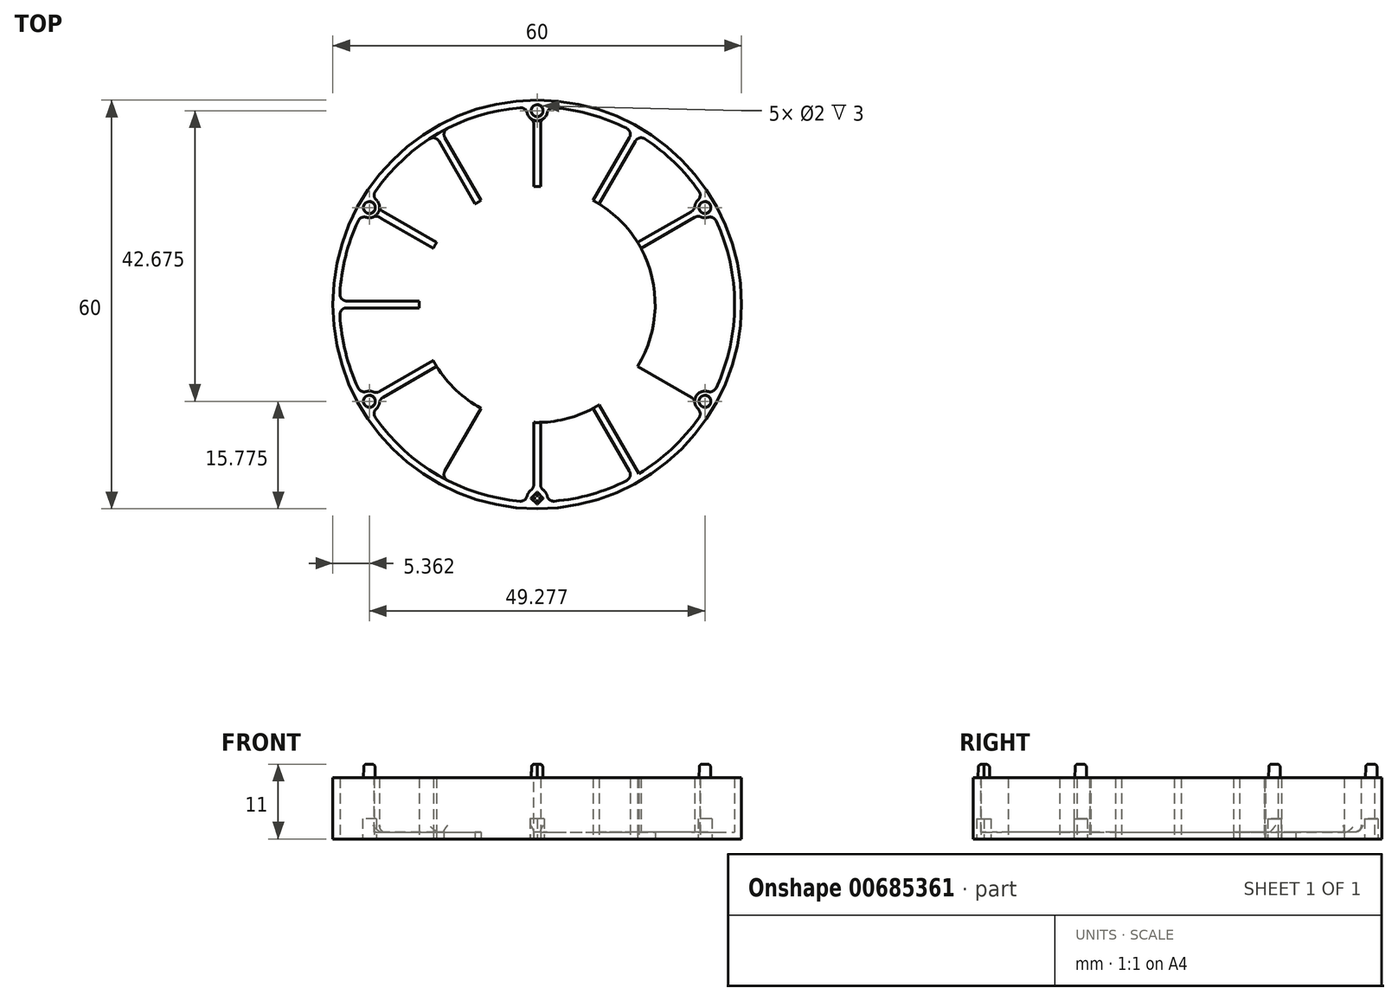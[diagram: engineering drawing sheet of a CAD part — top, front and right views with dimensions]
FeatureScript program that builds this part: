
annotation { "Feature Type Name" : "Feature", "Feature Type Description" : "" }
export const myFeature = defineFeature(function(context is Context, id is Id, definition is map)
    precondition{}
    {
        {
            var Q0;
            Q0=qCreatedBy(makeId("Top.planeOp"),FACE);
            var sketch = newSketch(context, id + "F0", { "sketchPlane" : qUnion([Q0])});
            skCircle(sketch, "E0", {"center": v(0, 0) * mm, "radius": 30 * mm});
            skCircle(sketch, "E1.0", {"center": v(0, 0) * mm, "radius": 29 * mm});
            skLineSegment(sketch, "E2.bottom", {"start": v(14.56, 26.23) * mm, "end": v(15.43, 25.73) * mm});
            skLineSegment(sketch, "E2.top", {"start": v(-15.43, -25.73) * mm, "end": v(-14.56, -26.23) * mm});
            skLineSegment(sketch, "E2.left", {"start": v(14.56, 26.23) * mm, "end": v(-15.43, -25.73) * mm});
            skLineSegment(sketch, "E2.right", {"start": v(15.43, 25.73) * mm, "end": v(-14.56, -26.23) * mm});
            skLineSegment(sketch, "E3.bottom", {"start": v(25.73, 15.43) * mm, "end": v(26.23, 14.56) * mm});
            skLineSegment(sketch, "E3.top", {"start": v(-26.23, -14.56) * mm, "end": v(-25.73, -15.43) * mm});
            skLineSegment(sketch, "E3.left", {"start": v(25.73, 15.43) * mm, "end": v(-26.23, -14.56) * mm});
            skLineSegment(sketch, "E3.right", {"start": v(26.23, 14.56) * mm, "end": v(-25.73, -15.43) * mm});
            skLineSegment(sketch, "E4", {"start": v(-38.35, 0) * mm, "end": v(39.17, 0) * mm, "construction": true});
            skLineSegment(sketch, "E5", {"start": v(0, 42.5) * mm, "end": v(0, -42.47) * mm, "construction": true});
            skLineSegment(sketch, "E6.bottom", {"start": v(-30, 0.5) * mm, "end": v(30, 0.5) * mm});
            skLineSegment(sketch, "E6.top", {"start": v(-30, -0.5) * mm, "end": v(30, -0.5) * mm});
            skLineSegment(sketch, "E6.left", {"start": v(-30, 0.5) * mm, "end": v(-30, -0.5) * mm});
            skLineSegment(sketch, "E6.right", {"start": v(30, 0.5) * mm, "end": v(30, -0.5) * mm});
            skLineSegment(sketch, "E7.bottom", {"start": v(-25.73, 15.43) * mm, "end": v(26.23, -14.56) * mm});
            skLineSegment(sketch, "E7.top", {"start": v(-26.23, 14.56) * mm, "end": v(25.73, -15.43) * mm});
            skLineSegment(sketch, "E7.left", {"start": v(-25.73, 15.43) * mm, "end": v(-26.23, 14.56) * mm});
            skLineSegment(sketch, "E7.right", {"start": v(26.23, -14.56) * mm, "end": v(25.73, -15.43) * mm});
            skLineSegment(sketch, "E8.bottom", {"start": v(-0.5, 30) * mm, "end": v(0.5, 30) * mm});
            skLineSegment(sketch, "E8.top", {"start": v(-0.5, -30) * mm, "end": v(0.5, -30) * mm});
            skLineSegment(sketch, "E8.left", {"start": v(-0.5, 30) * mm, "end": v(-0.5, -30) * mm});
            skLineSegment(sketch, "E8.right", {"start": v(0.5, 30) * mm, "end": v(0.5, -30) * mm});
            skLineSegment(sketch, "E9.bottom", {"start": v(-15.43, 25.73) * mm, "end": v(-14.56, 26.23) * mm});
            skLineSegment(sketch, "E9.top", {"start": v(14.56, -26.23) * mm, "end": v(15.43, -25.73) * mm});
            skLineSegment(sketch, "E9.left", {"start": v(-15.43, 25.73) * mm, "end": v(14.56, -26.23) * mm});
            skLineSegment(sketch, "E9.right", {"start": v(-14.56, 26.23) * mm, "end": v(15.43, -25.73) * mm});
            skCircle(sketch, "E10", {"center": v(0, 0) * mm, "radius": 17.33 * mm});
            skSolve(sketch);
        }
        {
            var Q0;
            Q0=qCreatedBy(makeId("Top.planeOp"),FACE);
            var sketch = newSketch(context, id + "F1", { "sketchPlane" : qUnion([Q0])});
            skCircle(sketch, "E11", {"center": v(0, 0) * mm, "radius": 30 * mm});
            skCircle(sketch, "E12", {"center": v(0, 0) * mm, "radius": 29 * mm});
            skSolve(sketch);
        }
        {
            var Q0;
            Q0=makeQuery(id+"F1.imprint","IMPRINT",FACE,{"disambiguationData":[TD([[makeQuery(id+"F1.imprint","IMPRINT",EDGE,{"derivedFrom":sQuery(id+"F1.wireOp",EDGE,"E11")}),1.0]])]});
            extrude(context, id + "F2", {"entities" : qUnion([Q0]), "depth" : 9 * mm, "offsetDistance" : 25 * mm});
        }
        {
            var Q0;
            {var subQ0=sQuery(id+"F0.wireOp",EDGE,"E2.right");var subQ1=sQuery(id+"F0.wireOp",EDGE,"E1.0");var subQ2=makeQuery(id+"F0.imprint","INTERSECT",VERTEX,{"disambiguationData":[OD(0.0)],"derivedFrom":[subQ1,subQ0]});Q0=makeQuery(id+"F0.imprint","IMPRINT",FACE,{"disambiguationData":[TD([[makeQuery(id+"F0.imprint","IMPRINT",EDGE,{"disambiguationData":[TD([[subQ2,-1.0]])],"derivedFrom":subQ1}),1.0]])]});}
            var Q1;
            {var subQ0=sQuery(id+"F0.wireOp",EDGE,"E8.left");var subQ1=sQuery(id+"F0.wireOp",EDGE,"E1.0");var subQ2=makeQuery(id+"F0.imprint","INTERSECT",VERTEX,{"disambiguationData":[OD(1.0)],"derivedFrom":[subQ1,subQ0]});Q1=makeQuery(id+"F0.imprint","IMPRINT",FACE,{"disambiguationData":[TD([[makeQuery(id+"F0.imprint","IMPRINT",EDGE,{"disambiguationData":[TD([[subQ2,-1.0]])],"derivedFrom":subQ1}),1.0]])]});}
            var Q2;
            {var subQ0=sQuery(id+"F0.wireOp",EDGE,"E3.left");var subQ1=sQuery(id+"F0.wireOp",EDGE,"E1.0");var subQ2=makeQuery(id+"F0.imprint","INTERSECT",VERTEX,{"disambiguationData":[OD(1.0)],"derivedFrom":[subQ1,subQ0]});Q2=makeQuery(id+"F0.imprint","IMPRINT",FACE,{"disambiguationData":[TD([[makeQuery(id+"F0.imprint","IMPRINT",EDGE,{"disambiguationData":[TD([[subQ2,-1.0]])],"derivedFrom":subQ1}),1.0]])]});}
            var Q3;
            {var subQ0=sQuery(id+"F0.wireOp",EDGE,"E3.right");var subQ1=sQuery(id+"F0.wireOp",EDGE,"E1.0");var subQ2=makeQuery(id+"F0.imprint","INTERSECT",VERTEX,{"disambiguationData":[OD(0.0)],"derivedFrom":[subQ1,subQ0]});Q3=makeQuery(id+"F0.imprint","IMPRINT",FACE,{"disambiguationData":[TD([[makeQuery(id+"F0.imprint","IMPRINT",EDGE,{"disambiguationData":[TD([[subQ2,-1.0]])],"derivedFrom":subQ1}),1.0]])]});}
            var Q4;
            {var subQ0=sQuery(id+"F0.wireOp",EDGE,"E9.left");var subQ1=sQuery(id+"F0.wireOp",EDGE,"E1.0");var subQ2=makeQuery(id+"F0.imprint","INTERSECT",VERTEX,{"disambiguationData":[OD(1.0)],"derivedFrom":[subQ1,subQ0]});Q4=makeQuery(id+"F0.imprint","IMPRINT",FACE,{"disambiguationData":[TD([[makeQuery(id+"F0.imprint","IMPRINT",EDGE,{"disambiguationData":[TD([[subQ2,-1.0]])],"derivedFrom":subQ1}),1.0]])]});}
            var Q5;
            {var subQ0=sQuery(id+"F0.wireOp",EDGE,"E6.bottom");var subQ1=sQuery(id+"F0.wireOp",EDGE,"E1.0");var subQ2=makeQuery(id+"F0.imprint","INTERSECT",VERTEX,{"disambiguationData":[OD(1.0)],"derivedFrom":[subQ1,subQ0]});Q5=makeQuery(id+"F0.imprint","IMPRINT",FACE,{"disambiguationData":[TD([[makeQuery(id+"F0.imprint","IMPRINT",EDGE,{"disambiguationData":[TD([[subQ2,-1.0]])],"derivedFrom":subQ1}),1.0]])]});}
            extrude(context, id + "F3", {"entities" : qUnion([Q0, Q1, Q2, Q3, Q4, Q5]), "operationType" : NewBodyOperationType.ADD, "depth" : 9 * mm, "offsetDistance" : 25 * mm});
        }
        {
            var Q0;
            Q0=makeQuery(id+"F1.imprint","IMPRINT",FACE,{"disambiguationData":[TD([[makeQuery(id+"F1.imprint","IMPRINT",EDGE,{"derivedFrom":sQuery(id+"F1.wireOp",EDGE,"E11")}),1.0]])]});
            var Q1;
            Q1=makeQuery(id+"F1.imprint","IMPRINT",FACE,{"disambiguationData":[TD([[makeQuery(id+"F1.imprint","IMPRINT",EDGE,{"derivedFrom":sQuery(id+"F1.wireOp",EDGE,"E12")}),1.0]])]});
            extrude(context, id + "F4", {"entities" : qUnion([Q0, Q1]), "operationType" : NewBodyOperationType.ADD, "depth" : 1 * mm, "offsetDistance" : 25 * mm});
        }
        {
            var Q0;
            {var subQ0=sQuery(id+"F0.wireOp",EDGE,"E9.right");var subQ1=sQuery(id+"F0.wireOp",EDGE,"E1.0");var subQ2=makeQuery(id+"F0.imprint","INTERSECT",VERTEX,{"disambiguationData":[OD(1.0)],"derivedFrom":[subQ1,subQ0]});Q0=makeQuery(id+"F0.imprint","IMPRINT",FACE,{"disambiguationData":[TD([[makeQuery(id+"F0.imprint","IMPRINT",EDGE,{"disambiguationData":[TD([[subQ2,-1.0]])],"derivedFrom":subQ1}),1.0]])]});}
            var Q1;
            {var subQ0=sQuery(id+"F0.wireOp",EDGE,"E2.left");var subQ1=sQuery(id+"F0.wireOp",EDGE,"E1.0");var subQ2=makeQuery(id+"F0.imprint","INTERSECT",VERTEX,{"disambiguationData":[OD(0.0)],"derivedFrom":[subQ1,subQ0]});Q1=makeQuery(id+"F0.imprint","IMPRINT",FACE,{"disambiguationData":[TD([[makeQuery(id+"F0.imprint","IMPRINT",EDGE,{"disambiguationData":[TD([[subQ2,-1.0]])],"derivedFrom":subQ1}),1.0]])]});}
            var Q2;
            {var subQ0=sQuery(id+"F0.wireOp",EDGE,"E2.right");var subQ1=sQuery(id+"F0.wireOp",EDGE,"E1.0");var subQ2=makeQuery(id+"F0.imprint","INTERSECT",VERTEX,{"disambiguationData":[OD(1.0)],"derivedFrom":[subQ1,subQ0]});Q2=makeQuery(id+"F0.imprint","IMPRINT",FACE,{"disambiguationData":[TD([[makeQuery(id+"F0.imprint","IMPRINT",EDGE,{"disambiguationData":[TD([[subQ2,-1.0]])],"derivedFrom":subQ1}),1.0]])]});}
            var Q3;
            {var subQ0=sQuery(id+"F0.wireOp",EDGE,"E8.left");var subQ1=sQuery(id+"F0.wireOp",EDGE,"E1.0");var subQ2=makeQuery(id+"F0.imprint","INTERSECT",VERTEX,{"disambiguationData":[OD(0.0)],"derivedFrom":[subQ1,subQ0]});Q3=makeQuery(id+"F0.imprint","IMPRINT",FACE,{"disambiguationData":[TD([[makeQuery(id+"F0.imprint","IMPRINT",EDGE,{"disambiguationData":[TD([[subQ2,-1.0]])],"derivedFrom":subQ1}),1.0]])]});}
            var Q4;
            {var subQ0=sQuery(id+"F0.wireOp",EDGE,"E9.left");var subQ1=sQuery(id+"F0.wireOp",EDGE,"E1.0");var subQ2=makeQuery(id+"F0.imprint","INTERSECT",VERTEX,{"disambiguationData":[OD(0.0)],"derivedFrom":[subQ1,subQ0]});Q4=makeQuery(id+"F0.imprint","IMPRINT",FACE,{"disambiguationData":[TD([[makeQuery(id+"F0.imprint","IMPRINT",EDGE,{"disambiguationData":[TD([[subQ2,-1.0]])],"derivedFrom":subQ1}),1.0]])]});}
            var Q5;
            {var subQ0=sQuery(id+"F0.wireOp",EDGE,"E7.top");var subQ1=sQuery(id+"F0.wireOp",EDGE,"E1.0");var subQ2=makeQuery(id+"F0.imprint","INTERSECT",VERTEX,{"disambiguationData":[OD(0.0)],"derivedFrom":[subQ1,subQ0]});Q5=makeQuery(id+"F0.imprint","IMPRINT",FACE,{"disambiguationData":[TD([[makeQuery(id+"F0.imprint","IMPRINT",EDGE,{"disambiguationData":[TD([[subQ2,-1.0]])],"derivedFrom":subQ1}),1.0]])]});}
            var Q6;
            {var subQ0=sQuery(id+"F0.wireOp",EDGE,"E6.top");var subQ1=sQuery(id+"F0.wireOp",EDGE,"E1.0");var subQ2=makeQuery(id+"F0.imprint","INTERSECT",VERTEX,{"disambiguationData":[OD(0.0)],"derivedFrom":[subQ1,subQ0]});Q6=makeQuery(id+"F0.imprint","IMPRINT",FACE,{"disambiguationData":[TD([[makeQuery(id+"F0.imprint","IMPRINT",EDGE,{"disambiguationData":[TD([[subQ2,-1.0]])],"derivedFrom":subQ1}),1.0]])]});}
            extrude(context, id + "F5", {"entities" : qUnion([Q0, Q1, Q2, Q3, Q4, Q5, Q6]), "operationType" : NewBodyOperationType.REMOVE, "depth" : 1 * mm, "offsetDistance" : 25 * mm});
        }
        {
            var Q0;
            Q0=qCreatedBy(makeId("Top.planeOp"),FACE);
            var sketch = newSketch(context, id + "F6", { "sketchPlane" : qUnion([Q0])});
            skCircle(sketch, "E13", {"center": v(0, 0) * mm, "radius": 28.45 * mm});
            skLineSegment(sketch, "E14", {"start": v(0, 28.45) * mm, "end": v(0, -28.45) * mm, "construction": true});
            skLineSegment(sketch, "E15", {"start": v(24.64, 14.22) * mm, "end": v(0, 0) * mm, "construction": true});
            skLineSegment(sketch, "E16", {"start": v(14.23, 24.64) * mm, "end": v(0, 0) * mm, "construction": true});
            skLineSegment(sketch, "E17", {"start": v(0, 0) * mm, "end": v(28.45, 0) * mm, "construction": true});
            skLineSegment(sketch, "E18", {"start": v(0, 0) * mm, "end": v(24.64, -14.22) * mm, "construction": true});
            skLineSegment(sketch, "E19", {"start": v(0, 0) * mm, "end": v(14.23, -24.64) * mm, "construction": true});
            skLineSegment(sketch, "E20", {"start": v(0, 0) * mm, "end": v(-14.23, 24.64) * mm, "construction": true});
            skLineSegment(sketch, "E21", {"start": v(0, 0) * mm, "end": v(-24.64, 14.22) * mm, "construction": true});
            skLineSegment(sketch, "E22", {"start": v(0, 0) * mm, "end": v(-28.45, 0) * mm, "construction": true});
            skLineSegment(sketch, "E23", {"start": v(0, 0) * mm, "end": v(-24.64, -14.23) * mm, "construction": true});
            skLineSegment(sketch, "E24", {"start": v(0, 0) * mm, "end": v(-14.22, -24.64) * mm, "construction": true});
            skCircle(sketch, "E25", {"center": v(0, 28.45) * mm, "radius": 1.5 * mm});
            skCircle(sketch, "E26", {"center": v(24.64, 14.22) * mm, "radius": 1.5 * mm});
            skCircle(sketch, "E27", {"center": v(24.64, -14.22) * mm, "radius": 1.5 * mm});
            skCircle(sketch, "E28", {"center": v(0, -28.45) * mm, "radius": 1.5 * mm});
            skCircle(sketch, "E29", {"center": v(-24.64, -14.23) * mm, "radius": 1.5 * mm});
            skCircle(sketch, "E30", {"center": v(-24.64, 14.22) * mm, "radius": 1.5 * mm});
            skCircle(sketch, "E31", {"center": v(-24.64, 14.22) * mm, "radius": 1 * mm});
            skCircle(sketch, "E32", {"center": v(0, 28.45) * mm, "radius": 1 * mm});
            skCircle(sketch, "E33", {"center": v(24.64, 14.22) * mm, "radius": 1 * mm});
            skCircle(sketch, "E34", {"center": v(24.64, -14.22) * mm, "radius": 1 * mm});
            skCircle(sketch, "E35", {"center": v(-24.64, -14.23) * mm, "radius": 1 * mm});
            skLineSegment(sketch, "E36.bottom", {"start": v(1.06, -28.45) * mm, "end": v(0, -29.51) * mm});
            skLineSegment(sketch, "E36.top", {"start": v(0, -27.39) * mm, "end": v(-1.06, -28.45) * mm});
            skLineSegment(sketch, "E36.left", {"start": v(1.06, -28.45) * mm, "end": v(0, -27.39) * mm});
            skLineSegment(sketch, "E36.right", {"start": v(0, -29.51) * mm, "end": v(-1.06, -28.45) * mm});
            skSolve(sketch);
        }
        {
            var Q0;
            {var subQ0=sQuery(id+"F6.wireOp",EDGE,"E30");var subQ1=sQuery(id+"F6.wireOp",EDGE,"E13");var subQ2=makeQuery(id+"F6.imprint","INTERSECT",VERTEX,{"disambiguationData":[OD(0.0)],"derivedFrom":[subQ1,subQ0]});Q0=makeQuery(id+"F6.imprint","IMPRINT",FACE,{"disambiguationData":[TD([[makeQuery(id+"F6.imprint","IMPRINT",EDGE,{"disambiguationData":[TD([[subQ2,-1.0]])],"derivedFrom":subQ1}),1.0]])]});}
            var Q1;
            {var subQ0=sQuery(id+"F6.wireOp",EDGE,"E30");var subQ1=sQuery(id+"F6.wireOp",EDGE,"E13");var subQ2=makeQuery(id+"F6.imprint","INTERSECT",VERTEX,{"disambiguationData":[OD(0.0)],"derivedFrom":[subQ1,subQ0]});Q1=makeQuery(id+"F6.imprint","IMPRINT",FACE,{"disambiguationData":[TD([[makeQuery(id+"F6.imprint","IMPRINT",EDGE,{"disambiguationData":[TD([[subQ2,-1.0]])],"derivedFrom":subQ1}),-1.0]])]});}
            var Q2;
            {var subQ0=sQuery(id+"F6.wireOp",EDGE,"E25");var subQ1=sQuery(id+"F6.wireOp",EDGE,"E13");var subQ2=makeQuery(id+"F6.imprint","INTERSECT",VERTEX,{"disambiguationData":[OD(0.0)],"derivedFrom":[subQ1,subQ0]});Q2=makeQuery(id+"F6.imprint","IMPRINT",FACE,{"disambiguationData":[TD([[makeQuery(id+"F6.imprint","IMPRINT",EDGE,{"disambiguationData":[TD([[subQ2,-1.0]])],"derivedFrom":subQ1}),1.0]])]});}
            var Q3;
            {var subQ0=sQuery(id+"F6.wireOp",EDGE,"E25");var subQ1=sQuery(id+"F6.wireOp",EDGE,"E13");var subQ2=makeQuery(id+"F6.imprint","INTERSECT",VERTEX,{"disambiguationData":[OD(0.0)],"derivedFrom":[subQ1,subQ0]});Q3=makeQuery(id+"F6.imprint","IMPRINT",FACE,{"disambiguationData":[TD([[makeQuery(id+"F6.imprint","IMPRINT",EDGE,{"disambiguationData":[TD([[subQ2,-1.0]])],"derivedFrom":subQ1}),-1.0]])]});}
            var Q4;
            {var subQ0=sQuery(id+"F6.wireOp",EDGE,"E26");var subQ1=sQuery(id+"F6.wireOp",EDGE,"E13");var subQ2=makeQuery(id+"F6.imprint","INTERSECT",VERTEX,{"disambiguationData":[OD(0.0)],"derivedFrom":[subQ1,subQ0]});Q4=makeQuery(id+"F6.imprint","IMPRINT",FACE,{"disambiguationData":[TD([[makeQuery(id+"F6.imprint","IMPRINT",EDGE,{"disambiguationData":[TD([[subQ2,-1.0]])],"derivedFrom":subQ1}),-1.0]])]});}
            var Q5;
            {var subQ0=sQuery(id+"F6.wireOp",EDGE,"E26");var subQ1=sQuery(id+"F6.wireOp",EDGE,"E13");var subQ2=makeQuery(id+"F6.imprint","INTERSECT",VERTEX,{"disambiguationData":[OD(0.0)],"derivedFrom":[subQ1,subQ0]});Q5=makeQuery(id+"F6.imprint","IMPRINT",FACE,{"disambiguationData":[TD([[makeQuery(id+"F6.imprint","IMPRINT",EDGE,{"disambiguationData":[TD([[subQ2,-1.0]])],"derivedFrom":subQ1}),1.0]])]});}
            var Q6;
            {var subQ0=sQuery(id+"F6.wireOp",EDGE,"E29");var subQ1=sQuery(id+"F6.wireOp",EDGE,"E13");var subQ2=makeQuery(id+"F6.imprint","INTERSECT",VERTEX,{"disambiguationData":[OD(0.0)],"derivedFrom":[subQ1,subQ0]});Q6=makeQuery(id+"F6.imprint","IMPRINT",FACE,{"disambiguationData":[TD([[makeQuery(id+"F6.imprint","IMPRINT",EDGE,{"disambiguationData":[TD([[subQ2,-1.0]])],"derivedFrom":subQ1}),1.0]])]});}
            var Q7;
            {var subQ0=sQuery(id+"F6.wireOp",EDGE,"E29");var subQ1=sQuery(id+"F6.wireOp",EDGE,"E13");var subQ2=makeQuery(id+"F6.imprint","INTERSECT",VERTEX,{"disambiguationData":[OD(0.0)],"derivedFrom":[subQ1,subQ0]});Q7=makeQuery(id+"F6.imprint","IMPRINT",FACE,{"disambiguationData":[TD([[makeQuery(id+"F6.imprint","IMPRINT",EDGE,{"disambiguationData":[TD([[subQ2,-1.0]])],"derivedFrom":subQ1}),-1.0]])]});}
            var Q8;
            {var subQ3=sQuery(id+"F6.wireOp",EDGE,"E13");var subQ5=sQuery(id+"F6.wireOp",EDGE,"E28");var subQ6=makeQuery(id+"F6.imprint","INTERSECT",VERTEX,{"disambiguationData":[OD(0.0)],"derivedFrom":[subQ3,subQ5]});Q8=makeQuery(id+"F6.imprint","IMPRINT",FACE,{"disambiguationData":[TD([[makeQuery(id+"F6.imprint","IMPRINT",EDGE,{"disambiguationData":[TD([[subQ6,-1.0]])],"derivedFrom":subQ3}),1.0]])]});}
            var Q9;
            {var subQ6=sQuery(id+"F6.wireOp",EDGE,"E36.bottom");Q9=makeQuery(id+"F6.imprint","IMPRINT",FACE,{"disambiguationData":[TD([[makeQuery(id+"F6.imprint","IMPRINT",EDGE,{"derivedFrom":subQ6}),1.0]])]});}
            var Q10;
            {var subQ0=sQuery(id+"F6.wireOp",EDGE,"E27");var subQ1=sQuery(id+"F6.wireOp",EDGE,"E13");var subQ2=makeQuery(id+"F6.imprint","INTERSECT",VERTEX,{"disambiguationData":[OD(0.0)],"derivedFrom":[subQ1,subQ0]});Q10=makeQuery(id+"F6.imprint","IMPRINT",FACE,{"disambiguationData":[TD([[makeQuery(id+"F6.imprint","IMPRINT",EDGE,{"disambiguationData":[TD([[subQ2,-1.0]])],"derivedFrom":subQ1}),-1.0]])]});}
            var Q11;
            {var subQ0=sQuery(id+"F6.wireOp",EDGE,"E27");var subQ1=sQuery(id+"F6.wireOp",EDGE,"E13");var subQ2=makeQuery(id+"F6.imprint","INTERSECT",VERTEX,{"disambiguationData":[OD(0.0)],"derivedFrom":[subQ1,subQ0]});Q11=makeQuery(id+"F6.imprint","IMPRINT",FACE,{"disambiguationData":[TD([[makeQuery(id+"F6.imprint","IMPRINT",EDGE,{"disambiguationData":[TD([[subQ2,-1.0]])],"derivedFrom":subQ1}),1.0]])]});}
            var Q12;
            {var subQ0=sQuery(id+"F6.wireOp",EDGE,"E31");var subQ1=sQuery(id+"F6.wireOp",EDGE,"E13");var subQ2=makeQuery(id+"F6.imprint","INTERSECT",VERTEX,{"disambiguationData":[OD(0.0)],"derivedFrom":[subQ1,subQ0]});Q12=makeQuery(id+"F6.imprint","IMPRINT",FACE,{"disambiguationData":[TD([[makeQuery(id+"F6.imprint","IMPRINT",EDGE,{"disambiguationData":[TD([[subQ2,-1.0]])],"derivedFrom":subQ1}),1.0]])]});}
            var Q13;
            {var subQ0=sQuery(id+"F6.wireOp",EDGE,"E31");var subQ1=sQuery(id+"F6.wireOp",EDGE,"E13");var subQ2=makeQuery(id+"F6.imprint","INTERSECT",VERTEX,{"disambiguationData":[OD(0.0)],"derivedFrom":[subQ1,subQ0]});Q13=makeQuery(id+"F6.imprint","IMPRINT",FACE,{"disambiguationData":[TD([[makeQuery(id+"F6.imprint","IMPRINT",EDGE,{"disambiguationData":[TD([[subQ2,-1.0]])],"derivedFrom":subQ1}),-1.0]])]});}
            var Q14;
            {var subQ0=sQuery(id+"F6.wireOp",EDGE,"E32");var subQ1=sQuery(id+"F6.wireOp",EDGE,"E13");var subQ2=makeQuery(id+"F6.imprint","INTERSECT",VERTEX,{"disambiguationData":[OD(0.0)],"derivedFrom":[subQ1,subQ0]});Q14=makeQuery(id+"F6.imprint","IMPRINT",FACE,{"disambiguationData":[TD([[makeQuery(id+"F6.imprint","IMPRINT",EDGE,{"disambiguationData":[TD([[subQ2,-1.0]])],"derivedFrom":subQ1}),-1.0]])]});}
            var Q15;
            {var subQ0=sQuery(id+"F6.wireOp",EDGE,"E32");var subQ1=sQuery(id+"F6.wireOp",EDGE,"E13");var subQ2=makeQuery(id+"F6.imprint","INTERSECT",VERTEX,{"disambiguationData":[OD(0.0)],"derivedFrom":[subQ1,subQ0]});Q15=makeQuery(id+"F6.imprint","IMPRINT",FACE,{"disambiguationData":[TD([[makeQuery(id+"F6.imprint","IMPRINT",EDGE,{"disambiguationData":[TD([[subQ2,-1.0]])],"derivedFrom":subQ1}),1.0]])]});}
            var Q16;
            {var subQ0=sQuery(id+"F6.wireOp",EDGE,"E33");var subQ1=sQuery(id+"F6.wireOp",EDGE,"E13");var subQ2=makeQuery(id+"F6.imprint","INTERSECT",VERTEX,{"disambiguationData":[OD(0.0)],"derivedFrom":[subQ1,subQ0]});Q16=makeQuery(id+"F6.imprint","IMPRINT",FACE,{"disambiguationData":[TD([[makeQuery(id+"F6.imprint","IMPRINT",EDGE,{"disambiguationData":[TD([[subQ2,-1.0]])],"derivedFrom":subQ1}),-1.0]])]});}
            var Q17;
            {var subQ0=sQuery(id+"F6.wireOp",EDGE,"E33");var subQ1=sQuery(id+"F6.wireOp",EDGE,"E13");var subQ2=makeQuery(id+"F6.imprint","INTERSECT",VERTEX,{"disambiguationData":[OD(0.0)],"derivedFrom":[subQ1,subQ0]});Q17=makeQuery(id+"F6.imprint","IMPRINT",FACE,{"disambiguationData":[TD([[makeQuery(id+"F6.imprint","IMPRINT",EDGE,{"disambiguationData":[TD([[subQ2,-1.0]])],"derivedFrom":subQ1}),1.0]])]});}
            var Q18;
            {var subQ0=sQuery(id+"F6.wireOp",EDGE,"E34");var subQ1=sQuery(id+"F6.wireOp",EDGE,"E13");var subQ2=makeQuery(id+"F6.imprint","INTERSECT",VERTEX,{"disambiguationData":[OD(0.0)],"derivedFrom":[subQ1,subQ0]});Q18=makeQuery(id+"F6.imprint","IMPRINT",FACE,{"disambiguationData":[TD([[makeQuery(id+"F6.imprint","IMPRINT",EDGE,{"disambiguationData":[TD([[subQ2,-1.0]])],"derivedFrom":subQ1}),-1.0]])]});}
            var Q19;
            {var subQ0=sQuery(id+"F6.wireOp",EDGE,"E34");var subQ1=sQuery(id+"F6.wireOp",EDGE,"E13");var subQ2=makeQuery(id+"F6.imprint","INTERSECT",VERTEX,{"disambiguationData":[OD(0.0)],"derivedFrom":[subQ1,subQ0]});Q19=makeQuery(id+"F6.imprint","IMPRINT",FACE,{"disambiguationData":[TD([[makeQuery(id+"F6.imprint","IMPRINT",EDGE,{"disambiguationData":[TD([[subQ2,-1.0]])],"derivedFrom":subQ1}),1.0]])]});}
            var Q20;
            {var subQ1=sQuery(id+"F6.wireOp",EDGE,"E36.bottom");Q20=makeQuery(id+"F6.imprint","IMPRINT",FACE,{"disambiguationData":[TD([[makeQuery(id+"F6.imprint","IMPRINT",EDGE,{"derivedFrom":subQ1}),-1.0]])]});}
            var Q21;
            {var subQ0=sQuery(id+"F6.wireOp",EDGE,"E35");var subQ1=sQuery(id+"F6.wireOp",EDGE,"E13");var subQ2=makeQuery(id+"F6.imprint","INTERSECT",VERTEX,{"disambiguationData":[OD(0.0)],"derivedFrom":[subQ1,subQ0]});Q21=makeQuery(id+"F6.imprint","IMPRINT",FACE,{"disambiguationData":[TD([[makeQuery(id+"F6.imprint","IMPRINT",EDGE,{"disambiguationData":[TD([[subQ2,-1.0]])],"derivedFrom":subQ1}),-1.0]])]});}
            var Q22;
            {var subQ0=sQuery(id+"F6.wireOp",EDGE,"E35");var subQ1=sQuery(id+"F6.wireOp",EDGE,"E13");var subQ2=makeQuery(id+"F6.imprint","INTERSECT",VERTEX,{"disambiguationData":[OD(0.0)],"derivedFrom":[subQ1,subQ0]});Q22=makeQuery(id+"F6.imprint","IMPRINT",FACE,{"disambiguationData":[TD([[makeQuery(id+"F6.imprint","IMPRINT",EDGE,{"disambiguationData":[TD([[subQ2,-1.0]])],"derivedFrom":subQ1}),1.0]])]});}
            var Q23;
            {var subQ0=sQuery(id+"F6.wireOp",EDGE,"E36.top");var subQ1=sQuery(id+"F6.wireOp",EDGE,"E13");var subQ2=makeQuery(id+"F6.imprint","INTERSECT",VERTEX,{"derivedFrom":[subQ1,subQ0]});Q23=makeQuery(id+"F6.imprint","IMPRINT",FACE,{"disambiguationData":[TD([[makeQuery(id+"F6.imprint","IMPRINT",EDGE,{"disambiguationData":[TD([[subQ2,-1.0]])],"derivedFrom":subQ1}),1.0]])]});}
            extrude(context, id + "F7", {"entities" : qUnion([Q0, Q1, Q2, Q3, Q4, Q5, Q6, Q7, Q8, Q9, Q10, Q11, Q12, Q13, Q14, Q15, Q16, Q17, Q18, Q19, Q20, Q21, Q22, Q23]), "operationType" : NewBodyOperationType.ADD, "depth" : 9 * mm, "offsetDistance" : 25 * mm});
        }
        {
            var Q0;
            {var subQ0=sQuery(id+"F0.wireOp",EDGE,"E8.right");var subQ1=sQuery(id+"F0.wireOp",EDGE,"E1.0");Q0=makeQuery(id+"F3.opExtrude","SWEPT_EDGE",EDGE,{"disambiguationData":[OSD([subQ1,subQ0]),TDD([makeQuery(id+"F0.imprint","INTERSECT",VERTEX,{"disambiguationData":[OD(1.0)],"derivedFrom":[subQ1,subQ0]})])]});}
            var Q1;
            {var subQ0=sQuery(id+"F0.wireOp",EDGE,"E2.left");var subQ1=sQuery(id+"F0.wireOp",EDGE,"E1.0");Q1=makeQuery(id+"F3.opExtrude","SWEPT_EDGE",EDGE,{"disambiguationData":[OSD([subQ1,subQ0]),TDD([makeQuery(id+"F0.imprint","INTERSECT",VERTEX,{"disambiguationData":[OD(1.0)],"derivedFrom":[subQ1,subQ0]})])]});}
            var Q2;
            {var subQ0=sQuery(id+"F0.wireOp",EDGE,"E3.left");var subQ1=sQuery(id+"F0.wireOp",EDGE,"E1.0");Q2=makeQuery(id+"F3.opExtrude","SWEPT_EDGE",EDGE,{"disambiguationData":[OSD([subQ1,subQ0]),TDD([makeQuery(id+"F0.imprint","INTERSECT",VERTEX,{"disambiguationData":[OD(1.0)],"derivedFrom":[subQ1,subQ0]})])]});}
            var Q3;
            {var subQ0=sQuery(id+"F0.wireOp",EDGE,"E6.bottom");var subQ1=sQuery(id+"F0.wireOp",EDGE,"E1.0");Q3=makeQuery(id+"F3.opExtrude","SWEPT_EDGE",EDGE,{"disambiguationData":[OSD([subQ1,subQ0]),TDD([makeQuery(id+"F0.imprint","INTERSECT",VERTEX,{"disambiguationData":[OD(1.0)],"derivedFrom":[subQ1,subQ0]})])]});}
            var Q4;
            {var subQ0=sQuery(id+"F0.wireOp",EDGE,"E9.right");var subQ1=sQuery(id+"F0.wireOp",EDGE,"E1.0");Q4=makeQuery(id+"F3.opExtrude","SWEPT_EDGE",EDGE,{"disambiguationData":[OSD([subQ1,subQ0]),TDD([makeQuery(id+"F0.imprint","INTERSECT",VERTEX,{"disambiguationData":[OD(1.0)],"derivedFrom":[subQ1,subQ0]})])]});}
            var Q5;
            {var subQ0=sQuery(id+"F0.wireOp",EDGE,"E7.bottom");var subQ1=sQuery(id+"F0.wireOp",EDGE,"E1.0");Q5=makeQuery(id+"F3.opExtrude","SWEPT_EDGE",EDGE,{"disambiguationData":[OSD([subQ1,subQ0]),TDD([makeQuery(id+"F0.imprint","INTERSECT",VERTEX,{"disambiguationData":[OD(1.0)],"derivedFrom":[subQ1,subQ0]})])]});}
            var Q6;
            {var subQ0=sQuery(id+"F0.wireOp",EDGE,"E8.left");var subQ1=sQuery(id+"F0.wireOp",EDGE,"E1.0");Q6=makeQuery(id+"F3.opExtrude","SWEPT_EDGE",EDGE,{"disambiguationData":[OSD([subQ1,subQ0]),TDD([makeQuery(id+"F0.imprint","INTERSECT",VERTEX,{"disambiguationData":[OD(0.0)],"derivedFrom":[subQ1,subQ0]})])]});}
            var Q7;
            {var subQ0=sQuery(id+"F0.wireOp",EDGE,"E2.left");var subQ1=sQuery(id+"F0.wireOp",EDGE,"E1.0");Q7=makeQuery(id+"F3.opExtrude","SWEPT_EDGE",EDGE,{"disambiguationData":[OSD([subQ1,subQ0]),TDD([makeQuery(id+"F0.imprint","INTERSECT",VERTEX,{"disambiguationData":[OD(0.0)],"derivedFrom":[subQ1,subQ0]})])]});}
            var Q8;
            {var subQ0=sQuery(id+"F0.wireOp",EDGE,"E3.left");var subQ1=sQuery(id+"F0.wireOp",EDGE,"E1.0");Q8=makeQuery(id+"F3.opExtrude","SWEPT_EDGE",EDGE,{"disambiguationData":[OSD([subQ1,subQ0]),TDD([makeQuery(id+"F0.imprint","INTERSECT",VERTEX,{"disambiguationData":[OD(0.0)],"derivedFrom":[subQ1,subQ0]})])]});}
            var Q9;
            {var subQ0=sQuery(id+"F0.wireOp",EDGE,"E6.top");var subQ1=sQuery(id+"F0.wireOp",EDGE,"E1.0");Q9=makeQuery(id+"F3.opExtrude","SWEPT_EDGE",EDGE,{"disambiguationData":[OSD([subQ1,subQ0]),TDD([makeQuery(id+"F0.imprint","INTERSECT",VERTEX,{"disambiguationData":[OD(1.0)],"derivedFrom":[subQ1,subQ0]})])]});}
            var Q10;
            {var subQ0=sQuery(id+"F0.wireOp",EDGE,"E7.top");var subQ1=sQuery(id+"F0.wireOp",EDGE,"E1.0");Q10=makeQuery(id+"F3.opExtrude","SWEPT_EDGE",EDGE,{"disambiguationData":[OSD([subQ1,subQ0]),TDD([makeQuery(id+"F0.imprint","INTERSECT",VERTEX,{"disambiguationData":[OD(0.0)],"derivedFrom":[subQ1,subQ0]})])]});}
            var Q11;
            {var subQ0=sQuery(id+"F0.wireOp",EDGE,"E6.top");var subQ1=sQuery(id+"F0.wireOp",EDGE,"E1.0");Q11=makeQuery(id+"F3.opExtrude","SWEPT_EDGE",EDGE,{"disambiguationData":[OSD([subQ1,subQ0]),TDD([makeQuery(id+"F0.imprint","INTERSECT",VERTEX,{"disambiguationData":[OD(0.0)],"derivedFrom":[subQ1,subQ0]})])]});}
            var Q12;
            {var subQ0=sQuery(id+"F0.wireOp",EDGE,"E9.left");var subQ1=sQuery(id+"F0.wireOp",EDGE,"E1.0");Q12=makeQuery(id+"F3.opExtrude","SWEPT_EDGE",EDGE,{"disambiguationData":[OSD([subQ1,subQ0]),TDD([makeQuery(id+"F0.imprint","INTERSECT",VERTEX,{"disambiguationData":[OD(0.0)],"derivedFrom":[subQ1,subQ0]})])]});}
            var Q13;
            {var subQ0=sQuery(id+"F0.wireOp",EDGE,"E8.right");var subQ1=sQuery(id+"F0.wireOp",EDGE,"E1.0");Q13=makeQuery(id+"F3.opExtrude","SWEPT_EDGE",EDGE,{"disambiguationData":[OSD([subQ1,subQ0]),TDD([makeQuery(id+"F0.imprint","INTERSECT",VERTEX,{"disambiguationData":[OD(0.0)],"derivedFrom":[subQ1,subQ0]})])]});}
            var Q14;
            {var subQ0=sQuery(id+"F0.wireOp",EDGE,"E7.bottom");var subQ1=sQuery(id+"F0.wireOp",EDGE,"E1.0");Q14=makeQuery(id+"F3.opExtrude","SWEPT_EDGE",EDGE,{"disambiguationData":[OSD([subQ1,subQ0]),TDD([makeQuery(id+"F0.imprint","INTERSECT",VERTEX,{"disambiguationData":[OD(0.0)],"derivedFrom":[subQ1,subQ0]})])]});}
            var Q15;
            {var subQ0=sQuery(id+"F0.wireOp",EDGE,"E9.right");var subQ1=sQuery(id+"F0.wireOp",EDGE,"E1.0");Q15=makeQuery(id+"F3.opExtrude","SWEPT_EDGE",EDGE,{"disambiguationData":[OSD([subQ1,subQ0]),TDD([makeQuery(id+"F0.imprint","INTERSECT",VERTEX,{"disambiguationData":[OD(0.0)],"derivedFrom":[subQ1,subQ0]})])]});}
            var Q16;
            {var subQ0=sQuery(id+"F0.wireOp",EDGE,"E3.right");var subQ1=sQuery(id+"F0.wireOp",EDGE,"E1.0");Q16=makeQuery(id+"F3.opExtrude","SWEPT_EDGE",EDGE,{"disambiguationData":[OSD([subQ1,subQ0]),TDD([makeQuery(id+"F0.imprint","INTERSECT",VERTEX,{"disambiguationData":[OD(1.0)],"derivedFrom":[subQ1,subQ0]})])]});}
            var Q17;
            {var subQ0=sQuery(id+"F0.wireOp",EDGE,"E2.right");var subQ1=sQuery(id+"F0.wireOp",EDGE,"E1.0");Q17=makeQuery(id+"F3.opExtrude","SWEPT_EDGE",EDGE,{"disambiguationData":[OSD([subQ1,subQ0]),TDD([makeQuery(id+"F0.imprint","INTERSECT",VERTEX,{"disambiguationData":[OD(1.0)],"derivedFrom":[subQ1,subQ0]})])]});}
            var Q18;
            {var subQ0=sQuery(id+"F0.wireOp",EDGE,"E3.right");var subQ1=sQuery(id+"F0.wireOp",EDGE,"E1.0");Q18=makeQuery(id+"F3.opExtrude","SWEPT_EDGE",EDGE,{"disambiguationData":[OSD([subQ1,subQ0]),TDD([makeQuery(id+"F0.imprint","INTERSECT",VERTEX,{"disambiguationData":[OD(0.0)],"derivedFrom":[subQ1,subQ0]})])]});}
            var Q19;
            {var subQ0=sQuery(id+"F0.wireOp",EDGE,"E2.right");var subQ1=sQuery(id+"F0.wireOp",EDGE,"E1.0");Q19=makeQuery(id+"F3.opExtrude","SWEPT_EDGE",EDGE,{"disambiguationData":[OSD([subQ1,subQ0]),TDD([makeQuery(id+"F0.imprint","INTERSECT",VERTEX,{"disambiguationData":[OD(0.0)],"derivedFrom":[subQ1,subQ0]})])]});}
            var Q20;
            {var subQ0=sQuery(id+"F0.wireOp",EDGE,"E8.left");var subQ1=sQuery(id+"F0.wireOp",EDGE,"E1.0");Q20=makeQuery(id+"F3.opExtrude","SWEPT_EDGE",EDGE,{"disambiguationData":[OSD([subQ1,subQ0]),TDD([makeQuery(id+"F0.imprint","INTERSECT",VERTEX,{"disambiguationData":[OD(1.0)],"derivedFrom":[subQ1,subQ0]})])]});}
            var Q21;
            {var subQ0=sQuery(id+"F0.wireOp",EDGE,"E9.left");var subQ1=sQuery(id+"F0.wireOp",EDGE,"E1.0");Q21=makeQuery(id+"F3.opExtrude","SWEPT_EDGE",EDGE,{"disambiguationData":[OSD([subQ1,subQ0]),TDD([makeQuery(id+"F0.imprint","INTERSECT",VERTEX,{"disambiguationData":[OD(1.0)],"derivedFrom":[subQ1,subQ0]})])]});}
            var Q22;
            {var subQ0=sQuery(id+"F0.wireOp",EDGE,"E7.top");var subQ1=sQuery(id+"F0.wireOp",EDGE,"E1.0");Q22=makeQuery(id+"F3.opExtrude","SWEPT_EDGE",EDGE,{"disambiguationData":[OSD([subQ1,subQ0]),TDD([makeQuery(id+"F0.imprint","INTERSECT",VERTEX,{"disambiguationData":[OD(1.0)],"derivedFrom":[subQ1,subQ0]})])]});}
            var Q23;
            {var subQ0=sQuery(id+"F0.wireOp",EDGE,"E6.bottom");var subQ1=sQuery(id+"F0.wireOp",EDGE,"E1.0");Q23=makeQuery(id+"F3.opExtrude","SWEPT_EDGE",EDGE,{"disambiguationData":[OSD([subQ1,subQ0]),TDD([makeQuery(id+"F0.imprint","INTERSECT",VERTEX,{"disambiguationData":[OD(0.0)],"derivedFrom":[subQ1,subQ0]})])]});}
            var Q24;
            {var subQ17=sQuery(id+"F0.wireOp",EDGE,"E8.right");var subQ18=sQuery(id+"F1.wireOp",EDGE,"E12");Q24=makeQuery(id+"F7.boolean.opBoolean","INTERSECT",EDGE,{"derivedFrom":[makeQuery(id+"F3.boolean.opBoolean","SPLIT",FACE,{"disambiguationData":[TD([makeQuery(id+"F3.opExtrude","SWEPT_FACE",FACE,{"disambiguationData":[OSD([subQ17])]})])],"derivedFrom":makeQuery(id+"F2.opExtrude","SWEPT_FACE",FACE,{"disambiguationData":[OSD([subQ18])]})}),makeQuery(id+"F7.opExtrude","SWEPT_FACE",FACE,{"disambiguationData":[OSD([sQuery(id+"F6.wireOp",EDGE,"E28")])]})]});}
            var Q25;
            {var subQ0=sQuery(id+"F0.wireOp",EDGE,"E6.top");var subQ1=sQuery(id+"F0.wireOp",EDGE,"E1.0");var subQ16=sQuery(id+"F1.wireOp",EDGE,"E12");Q25=makeQuery(id+"F7.boolean.opBoolean","INTERSECT",EDGE,{"derivedFrom":[makeQuery(id+"F5.boolean.opBoolean","MERGE",FACE,{"derivedFrom":[makeQuery(id+"F3.boolean.opBoolean","SPLIT",FACE,{"disambiguationData":[TD([makeQuery(id+"F3.opExtrude","SWEPT_FACE",FACE,{"disambiguationData":[OSD([subQ0])]})])],"derivedFrom":makeQuery(id+"F2.opExtrude","SWEPT_FACE",FACE,{"disambiguationData":[OSD([subQ16])]})}),makeQuery(id+"F5.opExtrude","SWEPT_FACE",FACE,{"disambiguationData":[OSD([subQ1]),TDD([makeQuery(id+"F0.imprint","IMPRINT",EDGE,{"disambiguationData":[TD([[makeQuery(id+"F0.imprint","INTERSECT",VERTEX,{"disambiguationData":[OD(0.0)],"derivedFrom":[subQ1,subQ0]}),-1.0]])],"derivedFrom":subQ1})])]})]}),makeQuery(id+"F7.opExtrude","SWEPT_FACE",FACE,{"disambiguationData":[OSD([sQuery(id+"F6.wireOp",EDGE,"E29")])]})]});}
            var Q26;
            Q26=makeQuery(id+"F7.boolean.opBoolean","INTERSECT",EDGE,{"derivedFrom":[makeQuery(id+"F3.opExtrude","SWEPT_FACE",FACE,{"disambiguationData":[OSD([sQuery(id+"F0.wireOp",EDGE,"E8.right")])]}),makeQuery(id+"F7.opExtrude","SWEPT_FACE",FACE,{"disambiguationData":[OSD([sQuery(id+"F6.wireOp",EDGE,"E28")])]})]});
            var Q27;
            {var subQ0=sQuery(id+"F0.wireOp",EDGE,"E3.left");Q27=makeQuery(id+"F7.boolean.opBoolean","INTERSECT",EDGE,{"derivedFrom":[makeQuery(id+"F5.boolean.opBoolean","MERGE",FACE,{"derivedFrom":[makeQuery(id+"F3.opExtrude","SWEPT_FACE",FACE,{"disambiguationData":[OSD([subQ0]),TDD([makeQuery(id+"F0.imprint","IMPRINT",EDGE,{"disambiguationData":[TD([[makeQuery(id+"F0.imprint","INTERSECT",VERTEX,{"disambiguationData":[OD(1.0)],"derivedFrom":[sQuery(id+"F0.wireOp",EDGE,"E1.0"),subQ0]}),1.0]])],"derivedFrom":subQ0})])]}),makeQuery(id+"F5.opExtrude","SWEPT_FACE",FACE,{"disambiguationData":[OSD([subQ0])]})]}),makeQuery(id+"F7.opExtrude","SWEPT_FACE",FACE,{"disambiguationData":[OSD([sQuery(id+"F6.wireOp",EDGE,"E29")])]})]});}
            var Q28;
            {var subQ0=sQuery(id+"F0.wireOp",EDGE,"E9.right");var subQ1=sQuery(id+"F0.wireOp",EDGE,"E1.0");var subQ17=sQuery(id+"F1.wireOp",EDGE,"E12");Q28=makeQuery(id+"F7.boolean.opBoolean","INTERSECT",EDGE,{"disambiguationData":[OD(0.0)],"derivedFrom":[makeQuery(id+"F5.boolean.opBoolean","MERGE",FACE,{"derivedFrom":[makeQuery(id+"F3.boolean.opBoolean","SPLIT",FACE,{"disambiguationData":[TD([makeQuery(id+"F3.opExtrude","SWEPT_FACE",FACE,{"disambiguationData":[OSD([subQ0])]})])],"derivedFrom":makeQuery(id+"F2.opExtrude","SWEPT_FACE",FACE,{"disambiguationData":[OSD([subQ17])]})}),makeQuery(id+"F5.opExtrude","SWEPT_FACE",FACE,{"disambiguationData":[OSD([subQ1]),TDD([makeQuery(id+"F0.imprint","IMPRINT",EDGE,{"disambiguationData":[TD([[makeQuery(id+"F0.imprint","INTERSECT",VERTEX,{"disambiguationData":[OD(1.0)],"derivedFrom":[subQ1,subQ0]}),-1.0]])],"derivedFrom":subQ1})])]})]}),makeQuery(id+"F7.opExtrude","SWEPT_FACE",FACE,{"disambiguationData":[OSD([sQuery(id+"F6.wireOp",EDGE,"E27")])]})]});}
            var Q29;
            {var subQ0=sQuery(id+"F0.wireOp",EDGE,"E9.right");var subQ1=sQuery(id+"F0.wireOp",EDGE,"E1.0");var subQ17=sQuery(id+"F1.wireOp",EDGE,"E12");Q29=makeQuery(id+"F7.boolean.opBoolean","INTERSECT",EDGE,{"derivedFrom":[makeQuery(id+"F5.boolean.opBoolean","MERGE",FACE,{"derivedFrom":[makeQuery(id+"F3.boolean.opBoolean","SPLIT",FACE,{"disambiguationData":[TD([makeQuery(id+"F3.opExtrude","SWEPT_FACE",FACE,{"disambiguationData":[OSD([subQ0])]})])],"derivedFrom":makeQuery(id+"F2.opExtrude","SWEPT_FACE",FACE,{"disambiguationData":[OSD([subQ17])]})}),makeQuery(id+"F5.opExtrude","SWEPT_FACE",FACE,{"disambiguationData":[OSD([subQ1]),TDD([makeQuery(id+"F0.imprint","IMPRINT",EDGE,{"disambiguationData":[TD([[makeQuery(id+"F0.imprint","INTERSECT",VERTEX,{"disambiguationData":[OD(1.0)],"derivedFrom":[subQ1,subQ0]}),-1.0]])],"derivedFrom":subQ1})])]})]}),makeQuery(id+"F7.opExtrude","SWEPT_FACE",FACE,{"disambiguationData":[OSD([sQuery(id+"F6.wireOp",EDGE,"E26")])]})]});}
            var Q30;
            {var subQ0=sQuery(id+"F0.wireOp",EDGE,"E1.0");var subQ2=sQuery(id+"F0.wireOp",EDGE,"E9.left");var subQ3=sQuery(id+"F0.wireOp",EDGE,"E8.left");var subQ5=sQuery(id+"F0.wireOp",EDGE,"E2.left");var subQ20=sQuery(id+"F1.wireOp",EDGE,"E12");Q30=makeQuery(id+"F7.boolean.opBoolean","INTERSECT",EDGE,{"disambiguationData":[OD(1.0)],"derivedFrom":[makeQuery(id+"F5.boolean.opBoolean","MERGE",FACE,{"derivedFrom":[makeQuery(id+"F3.boolean.opBoolean","SPLIT",FACE,{"disambiguationData":[TD([makeQuery(id+"F3.opExtrude","SWEPT_FACE",FACE,{"disambiguationData":[OSD([subQ5])]})])],"derivedFrom":makeQuery(id+"F2.opExtrude","SWEPT_FACE",FACE,{"disambiguationData":[OSD([subQ20])]})}),makeQuery(id+"F5.opExtrude","SWEPT_FACE",FACE,{"disambiguationData":[OSD([subQ0]),TDD([makeQuery(id+"F0.imprint","IMPRINT",EDGE,{"disambiguationData":[TD([[makeQuery(id+"F0.imprint","INTERSECT",VERTEX,{"disambiguationData":[OD(0.0)],"derivedFrom":[subQ0,subQ5]}),-1.0]])],"derivedFrom":subQ0})])]}),makeQuery(id+"F5.opExtrude","SWEPT_FACE",FACE,{"disambiguationData":[OSD([subQ0]),TDD([makeQuery(id+"F0.imprint","IMPRINT",EDGE,{"disambiguationData":[TD([[makeQuery(id+"F0.imprint","INTERSECT",VERTEX,{"disambiguationData":[OD(0.0)],"derivedFrom":[subQ0,subQ3]}),-1.0]])],"derivedFrom":subQ0})])]}),makeQuery(id+"F5.opExtrude","SWEPT_FACE",FACE,{"disambiguationData":[OSD([subQ0]),TDD([makeQuery(id+"F0.imprint","IMPRINT",EDGE,{"disambiguationData":[TD([[makeQuery(id+"F0.imprint","INTERSECT",VERTEX,{"disambiguationData":[OD(0.0)],"derivedFrom":[subQ0,subQ2]}),-1.0]])],"derivedFrom":subQ0})])]}),makeQuery(id+"F5.opExtrude","SWEPT_FACE",FACE,{"disambiguationData":[OSD([subQ0]),TDD([makeQuery(id+"F0.imprint","IMPRINT",EDGE,{"disambiguationData":[TD([[makeQuery(id+"F0.imprint","INTERSECT",VERTEX,{"disambiguationData":[OD(0.0)],"derivedFrom":[subQ0,sQuery(id+"F0.wireOp",EDGE,"E7.top")]}),-1.0]])],"derivedFrom":subQ0})])]})]}),makeQuery(id+"F7.opExtrude","SWEPT_FACE",FACE,{"disambiguationData":[OSD([sQuery(id+"F6.wireOp",EDGE,"E25")])]})]});}
            var Q31;
            {var subQ0=sQuery(id+"F0.wireOp",EDGE,"E8.left");Q31=makeQuery(id+"F7.boolean.opBoolean","INTERSECT",EDGE,{"derivedFrom":[makeQuery(id+"F5.boolean.opBoolean","COPY",FACE,{"derivedFrom":makeQuery(id+"F5.opExtrude","SWEPT_FACE",FACE,{"disambiguationData":[OSD([subQ0]),TDD([makeQuery(id+"F0.imprint","IMPRINT",EDGE,{"disambiguationData":[TD([[makeQuery(id+"F0.imprint","INTERSECT",VERTEX,{"disambiguationData":[OD(0.0)],"derivedFrom":[sQuery(id+"F0.wireOp",EDGE,"E1.0"),subQ0]}),-1.0]])],"derivedFrom":subQ0})])]})}),makeQuery(id+"F7.opExtrude","SWEPT_FACE",FACE,{"disambiguationData":[OSD([sQuery(id+"F6.wireOp",EDGE,"E25")])]})]});}
            var Q32;
            {var subQ0=sQuery(id+"F0.wireOp",EDGE,"E3.left");Q32=makeQuery(id+"F7.boolean.opBoolean","INTERSECT",EDGE,{"derivedFrom":[makeQuery(id+"F3.opExtrude","SWEPT_FACE",FACE,{"disambiguationData":[OSD([subQ0]),TDD([makeQuery(id+"F0.imprint","IMPRINT",EDGE,{"disambiguationData":[TD([[makeQuery(id+"F0.imprint","INTERSECT",VERTEX,{"disambiguationData":[OD(0.0)],"derivedFrom":[sQuery(id+"F0.wireOp",EDGE,"E1.0"),subQ0]}),-1.0]])],"derivedFrom":subQ0})])]}),makeQuery(id+"F7.opExtrude","SWEPT_FACE",FACE,{"disambiguationData":[OSD([sQuery(id+"F6.wireOp",EDGE,"E26")])]})]});}
            var Q33;
            {var subQ14=sQuery(id+"F0.wireOp",EDGE,"E2.right");var subQ16=sQuery(id+"F1.wireOp",EDGE,"E12");Q33=makeQuery(id+"F7.boolean.opBoolean","INTERSECT",EDGE,{"derivedFrom":[makeQuery(id+"F3.boolean.opBoolean","SPLIT",FACE,{"disambiguationData":[TD([makeQuery(id+"F3.opExtrude","SWEPT_FACE",FACE,{"disambiguationData":[OSD([subQ14])]})])],"derivedFrom":makeQuery(id+"F2.opExtrude","SWEPT_FACE",FACE,{"disambiguationData":[OSD([subQ16])]})}),makeQuery(id+"F7.opExtrude","SWEPT_FACE",FACE,{"disambiguationData":[OSD([sQuery(id+"F6.wireOp",EDGE,"E26")])]})]});}
            var Q34;
            {var subQ0=sQuery(id+"F0.wireOp",EDGE,"E1.0");var subQ2=sQuery(id+"F0.wireOp",EDGE,"E9.left");var subQ3=sQuery(id+"F0.wireOp",EDGE,"E8.left");var subQ5=sQuery(id+"F0.wireOp",EDGE,"E2.left");var subQ20=sQuery(id+"F1.wireOp",EDGE,"E12");Q34=makeQuery(id+"F7.boolean.opBoolean","INTERSECT",EDGE,{"disambiguationData":[OD(0.0)],"derivedFrom":[makeQuery(id+"F5.boolean.opBoolean","MERGE",FACE,{"derivedFrom":[makeQuery(id+"F3.boolean.opBoolean","SPLIT",FACE,{"disambiguationData":[TD([makeQuery(id+"F3.opExtrude","SWEPT_FACE",FACE,{"disambiguationData":[OSD([subQ5])]})])],"derivedFrom":makeQuery(id+"F2.opExtrude","SWEPT_FACE",FACE,{"disambiguationData":[OSD([subQ20])]})}),makeQuery(id+"F5.opExtrude","SWEPT_FACE",FACE,{"disambiguationData":[OSD([subQ0]),TDD([makeQuery(id+"F0.imprint","IMPRINT",EDGE,{"disambiguationData":[TD([[makeQuery(id+"F0.imprint","INTERSECT",VERTEX,{"disambiguationData":[OD(0.0)],"derivedFrom":[subQ0,subQ5]}),-1.0]])],"derivedFrom":subQ0})])]}),makeQuery(id+"F5.opExtrude","SWEPT_FACE",FACE,{"disambiguationData":[OSD([subQ0]),TDD([makeQuery(id+"F0.imprint","IMPRINT",EDGE,{"disambiguationData":[TD([[makeQuery(id+"F0.imprint","INTERSECT",VERTEX,{"disambiguationData":[OD(0.0)],"derivedFrom":[subQ0,subQ3]}),-1.0]])],"derivedFrom":subQ0})])]}),makeQuery(id+"F5.opExtrude","SWEPT_FACE",FACE,{"disambiguationData":[OSD([subQ0]),TDD([makeQuery(id+"F0.imprint","IMPRINT",EDGE,{"disambiguationData":[TD([[makeQuery(id+"F0.imprint","INTERSECT",VERTEX,{"disambiguationData":[OD(0.0)],"derivedFrom":[subQ0,subQ2]}),-1.0]])],"derivedFrom":subQ0})])]}),makeQuery(id+"F5.opExtrude","SWEPT_FACE",FACE,{"disambiguationData":[OSD([subQ0]),TDD([makeQuery(id+"F0.imprint","IMPRINT",EDGE,{"disambiguationData":[TD([[makeQuery(id+"F0.imprint","INTERSECT",VERTEX,{"disambiguationData":[OD(0.0)],"derivedFrom":[subQ0,sQuery(id+"F0.wireOp",EDGE,"E7.top")]}),-1.0]])],"derivedFrom":subQ0})])]})]}),makeQuery(id+"F7.opExtrude","SWEPT_FACE",FACE,{"disambiguationData":[OSD([sQuery(id+"F6.wireOp",EDGE,"E30")])]})]});}
            var Q35;
            {var subQ0=sQuery(id+"F0.wireOp",EDGE,"E2.right");var subQ1=sQuery(id+"F0.wireOp",EDGE,"E1.0");var subQ2=sQuery(id+"F0.wireOp",EDGE,"E8.left");var subQ17=sQuery(id+"F1.wireOp",EDGE,"E12");Q35=makeQuery(id+"F7.boolean.opBoolean","INTERSECT",EDGE,{"derivedFrom":[makeQuery(id+"F5.boolean.opBoolean","MERGE",FACE,{"derivedFrom":[makeQuery(id+"F3.boolean.opBoolean","SPLIT",FACE,{"disambiguationData":[TD([makeQuery(id+"F3.opExtrude","SWEPT_FACE",FACE,{"disambiguationData":[OSD([subQ2])]})])],"derivedFrom":makeQuery(id+"F2.opExtrude","SWEPT_FACE",FACE,{"disambiguationData":[OSD([subQ17])]})}),makeQuery(id+"F5.opExtrude","SWEPT_FACE",FACE,{"disambiguationData":[OSD([subQ1]),TDD([makeQuery(id+"F0.imprint","IMPRINT",EDGE,{"disambiguationData":[TD([[makeQuery(id+"F0.imprint","INTERSECT",VERTEX,{"disambiguationData":[OD(1.0)],"derivedFrom":[subQ1,subQ0]}),-1.0]])],"derivedFrom":subQ1})])]})]}),makeQuery(id+"F7.opExtrude","SWEPT_FACE",FACE,{"disambiguationData":[OSD([sQuery(id+"F6.wireOp",EDGE,"E29")])]})]});}
            var Q36;
            {var subQ0=sQuery(id+"F0.wireOp",EDGE,"E1.0");var subQ2=sQuery(id+"F0.wireOp",EDGE,"E9.left");var subQ3=sQuery(id+"F0.wireOp",EDGE,"E8.left");var subQ5=sQuery(id+"F0.wireOp",EDGE,"E2.left");var subQ20=sQuery(id+"F1.wireOp",EDGE,"E12");Q36=makeQuery(id+"F7.boolean.opBoolean","INTERSECT",EDGE,{"disambiguationData":[OD(1.0)],"derivedFrom":[makeQuery(id+"F5.boolean.opBoolean","MERGE",FACE,{"derivedFrom":[makeQuery(id+"F3.boolean.opBoolean","SPLIT",FACE,{"disambiguationData":[TD([makeQuery(id+"F3.opExtrude","SWEPT_FACE",FACE,{"disambiguationData":[OSD([subQ5])]})])],"derivedFrom":makeQuery(id+"F2.opExtrude","SWEPT_FACE",FACE,{"disambiguationData":[OSD([subQ20])]})}),makeQuery(id+"F5.opExtrude","SWEPT_FACE",FACE,{"disambiguationData":[OSD([subQ0]),TDD([makeQuery(id+"F0.imprint","IMPRINT",EDGE,{"disambiguationData":[TD([[makeQuery(id+"F0.imprint","INTERSECT",VERTEX,{"disambiguationData":[OD(0.0)],"derivedFrom":[subQ0,subQ5]}),-1.0]])],"derivedFrom":subQ0})])]}),makeQuery(id+"F5.opExtrude","SWEPT_FACE",FACE,{"disambiguationData":[OSD([subQ0]),TDD([makeQuery(id+"F0.imprint","IMPRINT",EDGE,{"disambiguationData":[TD([[makeQuery(id+"F0.imprint","INTERSECT",VERTEX,{"disambiguationData":[OD(0.0)],"derivedFrom":[subQ0,subQ3]}),-1.0]])],"derivedFrom":subQ0})])]}),makeQuery(id+"F5.opExtrude","SWEPT_FACE",FACE,{"disambiguationData":[OSD([subQ0]),TDD([makeQuery(id+"F0.imprint","IMPRINT",EDGE,{"disambiguationData":[TD([[makeQuery(id+"F0.imprint","INTERSECT",VERTEX,{"disambiguationData":[OD(0.0)],"derivedFrom":[subQ0,subQ2]}),-1.0]])],"derivedFrom":subQ0})])]}),makeQuery(id+"F5.opExtrude","SWEPT_FACE",FACE,{"disambiguationData":[OSD([subQ0]),TDD([makeQuery(id+"F0.imprint","IMPRINT",EDGE,{"disambiguationData":[TD([[makeQuery(id+"F0.imprint","INTERSECT",VERTEX,{"disambiguationData":[OD(0.0)],"derivedFrom":[subQ0,sQuery(id+"F0.wireOp",EDGE,"E7.top")]}),-1.0]])],"derivedFrom":subQ0})])]})]}),makeQuery(id+"F7.opExtrude","SWEPT_FACE",FACE,{"disambiguationData":[OSD([sQuery(id+"F6.wireOp",EDGE,"E30")])]})]});}
            var Q37;
            {var subQ0=sQuery(id+"F0.wireOp",EDGE,"E1.0");var subQ2=sQuery(id+"F0.wireOp",EDGE,"E9.left");var subQ3=sQuery(id+"F0.wireOp",EDGE,"E8.left");var subQ5=sQuery(id+"F0.wireOp",EDGE,"E2.left");var subQ20=sQuery(id+"F1.wireOp",EDGE,"E12");Q37=makeQuery(id+"F7.boolean.opBoolean","INTERSECT",EDGE,{"disambiguationData":[OD(0.0)],"derivedFrom":[makeQuery(id+"F5.boolean.opBoolean","MERGE",FACE,{"derivedFrom":[makeQuery(id+"F3.boolean.opBoolean","SPLIT",FACE,{"disambiguationData":[TD([makeQuery(id+"F3.opExtrude","SWEPT_FACE",FACE,{"disambiguationData":[OSD([subQ5])]})])],"derivedFrom":makeQuery(id+"F2.opExtrude","SWEPT_FACE",FACE,{"disambiguationData":[OSD([subQ20])]})}),makeQuery(id+"F5.opExtrude","SWEPT_FACE",FACE,{"disambiguationData":[OSD([subQ0]),TDD([makeQuery(id+"F0.imprint","IMPRINT",EDGE,{"disambiguationData":[TD([[makeQuery(id+"F0.imprint","INTERSECT",VERTEX,{"disambiguationData":[OD(0.0)],"derivedFrom":[subQ0,subQ5]}),-1.0]])],"derivedFrom":subQ0})])]}),makeQuery(id+"F5.opExtrude","SWEPT_FACE",FACE,{"disambiguationData":[OSD([subQ0]),TDD([makeQuery(id+"F0.imprint","IMPRINT",EDGE,{"disambiguationData":[TD([[makeQuery(id+"F0.imprint","INTERSECT",VERTEX,{"disambiguationData":[OD(0.0)],"derivedFrom":[subQ0,subQ3]}),-1.0]])],"derivedFrom":subQ0})])]}),makeQuery(id+"F5.opExtrude","SWEPT_FACE",FACE,{"disambiguationData":[OSD([subQ0]),TDD([makeQuery(id+"F0.imprint","IMPRINT",EDGE,{"disambiguationData":[TD([[makeQuery(id+"F0.imprint","INTERSECT",VERTEX,{"disambiguationData":[OD(0.0)],"derivedFrom":[subQ0,subQ2]}),-1.0]])],"derivedFrom":subQ0})])]}),makeQuery(id+"F5.opExtrude","SWEPT_FACE",FACE,{"disambiguationData":[OSD([subQ0]),TDD([makeQuery(id+"F0.imprint","IMPRINT",EDGE,{"disambiguationData":[TD([[makeQuery(id+"F0.imprint","INTERSECT",VERTEX,{"disambiguationData":[OD(0.0)],"derivedFrom":[subQ0,sQuery(id+"F0.wireOp",EDGE,"E7.top")]}),-1.0]])],"derivedFrom":subQ0})])]})]}),makeQuery(id+"F7.opExtrude","SWEPT_FACE",FACE,{"disambiguationData":[OSD([sQuery(id+"F6.wireOp",EDGE,"E25")])]})]});}
            var Q38;
            {var subQ0=sQuery(id+"F0.wireOp",EDGE,"E7.top");Q38=makeQuery(id+"F7.boolean.opBoolean","INTERSECT",EDGE,{"derivedFrom":[makeQuery(id+"F5.boolean.opBoolean","COPY",FACE,{"derivedFrom":makeQuery(id+"F5.opExtrude","SWEPT_FACE",FACE,{"disambiguationData":[OSD([subQ0]),TDD([makeQuery(id+"F0.imprint","IMPRINT",EDGE,{"disambiguationData":[TD([[makeQuery(id+"F0.imprint","INTERSECT",VERTEX,{"disambiguationData":[OD(0.0)],"derivedFrom":[sQuery(id+"F0.wireOp",EDGE,"E1.0"),subQ0]}),-1.0]])],"derivedFrom":subQ0})])]})}),makeQuery(id+"F7.opExtrude","SWEPT_FACE",FACE,{"disambiguationData":[OSD([sQuery(id+"F6.wireOp",EDGE,"E30")])]})]});}
            var Q39;
            Q39=makeQuery(id+"F7.boolean.opBoolean","INTERSECT",EDGE,{"derivedFrom":[makeQuery(id+"F4.opExtrude","CAP_FACE",FACE,{"disambiguationData":[OSD([sQuery(id+"F1.wireOp",EDGE,"E11")])],"isStart":false}),makeQuery(id+"F7.opExtrude","SWEPT_FACE",FACE,{"disambiguationData":[OSD([sQuery(id+"F6.wireOp",EDGE,"E30")])]})]});
            var Q40;
            Q40=makeQuery(id+"F7.boolean.opBoolean","INTERSECT",EDGE,{"derivedFrom":[makeQuery(id+"F5.boolean.opBoolean","COPY",FACE,{"derivedFrom":makeQuery(id+"F5.opExtrude","SWEPT_FACE",FACE,{"disambiguationData":[OSD([sQuery(id+"F0.wireOp",EDGE,"E7.bottom")])]})}),makeQuery(id+"F7.opExtrude","SWEPT_FACE",FACE,{"disambiguationData":[OSD([sQuery(id+"F6.wireOp",EDGE,"E30")])]})]});
            var Q41;
            {var subQ0=sQuery(id+"F0.wireOp",EDGE,"E9.right");var subQ1=sQuery(id+"F0.wireOp",EDGE,"E1.0");Q41=makeQuery(id+"F5.boolean.opBoolean","COPY",EDGE,{"derivedFrom":makeQuery(id+"F5.opExtrude","SWEPT_EDGE",EDGE,{"disambiguationData":[OSD([subQ1,subQ0]),TDD([makeQuery(id+"F0.imprint","INTERSECT",VERTEX,{"disambiguationData":[OD(0.0)],"derivedFrom":[subQ1,subQ0]})])]})});}
            var Q42;
            {var subQ0=sQuery(id+"F0.wireOp",EDGE,"E2.left");var subQ6=sQuery(id+"F1.wireOp",EDGE,"E11");var subQ7=makeQuery(id+"F4.opExtrude","CAP_FACE",FACE,{"disambiguationData":[OSD([subQ6])],"isStart":false});var subQ8=sQuery(id+"F1.wireOp",EDGE,"E12");var subQ9=makeQuery(id+"F2.opExtrude","SWEPT_FACE",FACE,{"disambiguationData":[OSD([subQ8])]});var subQ11=sQuery(id+"F0.wireOp",EDGE,"E9.left");Q42=makeQuery(id+"F5.boolean.opBoolean","SPLIT",EDGE,{"disambiguationData":[TD([makeQuery(id+"F5.opExtrude","SWEPT_FACE",FACE,{"disambiguationData":[OSD([subQ11])]})])],"derivedFrom":makeQuery(id+"F4.boolean.opBoolean","INTERSECT",EDGE,{"derivedFrom":[makeQuery(id+"F3.boolean.opBoolean","SPLIT",FACE,{"disambiguationData":[TD([makeQuery(id+"F3.opExtrude","SWEPT_FACE",FACE,{"disambiguationData":[OSD([subQ0])]})])],"derivedFrom":subQ9}),subQ7]})});}
            var Q43;
            Q43=makeQuery(id+"F5.boolean.opBoolean","COPY",EDGE,{"derivedFrom":makeQuery(id+"F5.opExtrude","SWEPT_EDGE",EDGE,{"disambiguationData":[OSD([sQuery(id+"F0.wireOp",EDGE,"E1.0"),sQuery(id+"F0.wireOp",EDGE,"E9.left")])]})});
            var Q44;
            Q44=makeQuery(id+"F7.boolean.opBoolean","INTERSECT",EDGE,{"derivedFrom":[makeQuery(id+"F5.boolean.opBoolean","COPY",FACE,{"derivedFrom":makeQuery(id+"F5.opExtrude","SWEPT_FACE",FACE,{"disambiguationData":[OSD([sQuery(id+"F0.wireOp",EDGE,"E8.right")])]})}),makeQuery(id+"F7.opExtrude","SWEPT_FACE",FACE,{"disambiguationData":[OSD([sQuery(id+"F6.wireOp",EDGE,"E25")])]})]});
            var Q45;
            Q45=makeQuery(id+"F7.boolean.opBoolean","INTERSECT",EDGE,{"derivedFrom":[makeQuery(id+"F4.opExtrude","CAP_FACE",FACE,{"disambiguationData":[OSD([sQuery(id+"F1.wireOp",EDGE,"E11")])],"isStart":false}),makeQuery(id+"F7.opExtrude","SWEPT_FACE",FACE,{"disambiguationData":[OSD([sQuery(id+"F6.wireOp",EDGE,"E25")])]})]});
            var Q46;
            {var subQ0=sQuery(id+"F0.wireOp",EDGE,"E3.right");Q46=makeQuery(id+"F7.boolean.opBoolean","INTERSECT",EDGE,{"derivedFrom":[makeQuery(id+"F3.opExtrude","SWEPT_FACE",FACE,{"disambiguationData":[OSD([subQ0]),TDD([makeQuery(id+"F0.imprint","IMPRINT",EDGE,{"disambiguationData":[TD([[makeQuery(id+"F0.imprint","INTERSECT",VERTEX,{"disambiguationData":[OD(0.0)],"derivedFrom":[sQuery(id+"F0.wireOp",EDGE,"E1.0"),subQ0]}),-1.0]])],"derivedFrom":subQ0})])]}),makeQuery(id+"F7.opExtrude","SWEPT_FACE",FACE,{"disambiguationData":[OSD([sQuery(id+"F6.wireOp",EDGE,"E26")])]})]});}
            var Q47;
            {var subQ0=sQuery(id+"F0.wireOp",EDGE,"E9.right");var subQ1=sQuery(id+"F0.wireOp",EDGE,"E1.0");var subQ17=sQuery(id+"F1.wireOp",EDGE,"E12");Q47=makeQuery(id+"F7.boolean.opBoolean","INTERSECT",EDGE,{"disambiguationData":[OD(1.0)],"derivedFrom":[makeQuery(id+"F5.boolean.opBoolean","MERGE",FACE,{"derivedFrom":[makeQuery(id+"F3.boolean.opBoolean","SPLIT",FACE,{"disambiguationData":[TD([makeQuery(id+"F3.opExtrude","SWEPT_FACE",FACE,{"disambiguationData":[OSD([subQ0])]})])],"derivedFrom":makeQuery(id+"F2.opExtrude","SWEPT_FACE",FACE,{"disambiguationData":[OSD([subQ17])]})}),makeQuery(id+"F5.opExtrude","SWEPT_FACE",FACE,{"disambiguationData":[OSD([subQ1]),TDD([makeQuery(id+"F0.imprint","IMPRINT",EDGE,{"disambiguationData":[TD([[makeQuery(id+"F0.imprint","INTERSECT",VERTEX,{"disambiguationData":[OD(1.0)],"derivedFrom":[subQ1,subQ0]}),-1.0]])],"derivedFrom":subQ1})])]})]}),makeQuery(id+"F7.opExtrude","SWEPT_FACE",FACE,{"disambiguationData":[OSD([sQuery(id+"F6.wireOp",EDGE,"E27")])]})]});}
            var Q48;
            {var subQ0=sQuery(id+"F0.wireOp",EDGE,"E7.top");Q48=makeQuery(id+"F7.boolean.opBoolean","INTERSECT",EDGE,{"derivedFrom":[makeQuery(id+"F5.boolean.opBoolean","COPY",FACE,{"derivedFrom":makeQuery(id+"F5.opExtrude","SWEPT_FACE",FACE,{"disambiguationData":[OSD([subQ0]),TDD([makeQuery(id+"F0.imprint","IMPRINT",EDGE,{"disambiguationData":[TD([[makeQuery(id+"F0.imprint","INTERSECT",VERTEX,{"disambiguationData":[OD(1.0)],"derivedFrom":[sQuery(id+"F0.wireOp",EDGE,"E1.0"),subQ0]}),1.0]])],"derivedFrom":subQ0})])]})}),makeQuery(id+"F7.opExtrude","SWEPT_FACE",FACE,{"disambiguationData":[OSD([sQuery(id+"F6.wireOp",EDGE,"E27")])]})]});}
            var Q49;
            {var subQ0=sQuery(id+"F0.wireOp",EDGE,"E2.right");var subQ1=sQuery(id+"F0.wireOp",EDGE,"E1.0");var subQ2=sQuery(id+"F0.wireOp",EDGE,"E8.left");var subQ17=sQuery(id+"F1.wireOp",EDGE,"E12");Q49=makeQuery(id+"F7.boolean.opBoolean","INTERSECT",EDGE,{"derivedFrom":[makeQuery(id+"F5.boolean.opBoolean","MERGE",FACE,{"derivedFrom":[makeQuery(id+"F3.boolean.opBoolean","SPLIT",FACE,{"disambiguationData":[TD([makeQuery(id+"F3.opExtrude","SWEPT_FACE",FACE,{"disambiguationData":[OSD([subQ2])]})])],"derivedFrom":makeQuery(id+"F2.opExtrude","SWEPT_FACE",FACE,{"disambiguationData":[OSD([subQ17])]})}),makeQuery(id+"F5.opExtrude","SWEPT_FACE",FACE,{"disambiguationData":[OSD([subQ1]),TDD([makeQuery(id+"F0.imprint","IMPRINT",EDGE,{"disambiguationData":[TD([[makeQuery(id+"F0.imprint","INTERSECT",VERTEX,{"disambiguationData":[OD(1.0)],"derivedFrom":[subQ1,subQ0]}),-1.0]])],"derivedFrom":subQ1})])]})]}),makeQuery(id+"F7.opExtrude","SWEPT_FACE",FACE,{"disambiguationData":[OSD([sQuery(id+"F6.wireOp",EDGE,"E28")])]})]});}
            var Q50;
            {var subQ0=sQuery(id+"F0.wireOp",EDGE,"E8.left");Q50=makeQuery(id+"F7.boolean.opBoolean","INTERSECT",EDGE,{"derivedFrom":[makeQuery(id+"F5.boolean.opBoolean","MERGE",FACE,{"derivedFrom":[makeQuery(id+"F3.opExtrude","SWEPT_FACE",FACE,{"disambiguationData":[OSD([subQ0])]}),makeQuery(id+"F5.opExtrude","SWEPT_FACE",FACE,{"disambiguationData":[OSD([subQ0]),TDD([makeQuery(id+"F0.imprint","IMPRINT",EDGE,{"disambiguationData":[TD([[makeQuery(id+"F0.imprint","INTERSECT",VERTEX,{"disambiguationData":[OD(1.0)],"derivedFrom":[sQuery(id+"F0.wireOp",EDGE,"E1.0"),subQ0]}),1.0]])],"derivedFrom":subQ0})])]})]}),makeQuery(id+"F7.opExtrude","SWEPT_FACE",FACE,{"disambiguationData":[OSD([sQuery(id+"F6.wireOp",EDGE,"E28")])]})]});}
            var Q51;
            Q51=makeQuery(id+"F5.boolean.opBoolean","COPY",EDGE,{"derivedFrom":makeQuery(id+"F5.opExtrude","SWEPT_EDGE",EDGE,{"disambiguationData":[OSD([sQuery(id+"F0.wireOp",EDGE,"E1.0"),sQuery(id+"F0.wireOp",EDGE,"E2.right")])]})});
            var Q52;
            {var subQ0=sQuery(id+"F0.wireOp",EDGE,"E3.right");Q52=makeQuery(id+"F7.boolean.opBoolean","INTERSECT",EDGE,{"derivedFrom":[makeQuery(id+"F3.opExtrude","SWEPT_FACE",FACE,{"disambiguationData":[OSD([subQ0]),TDD([makeQuery(id+"F0.imprint","IMPRINT",EDGE,{"disambiguationData":[TD([[makeQuery(id+"F0.imprint","INTERSECT",VERTEX,{"disambiguationData":[OD(1.0)],"derivedFrom":[sQuery(id+"F0.wireOp",EDGE,"E1.0"),subQ0]}),1.0]])],"derivedFrom":subQ0})])]}),makeQuery(id+"F7.opExtrude","SWEPT_FACE",FACE,{"disambiguationData":[OSD([sQuery(id+"F6.wireOp",EDGE,"E29")])]})]});}
            fillet(context, id + "F8", {"entities" : qUnion([Q0, Q1, Q2, Q3, Q4, Q5, Q6, Q7, Q8, Q9, Q10, Q11, Q12, Q13, Q14, Q15, Q16, Q17, Q18, Q19, Q20, Q21, Q22, Q23, Q24, Q25, Q26, Q27, Q28, Q29, Q30, Q31, Q32, Q33, Q34, Q35, Q36, Q37, Q38, Q39, Q40, Q41, Q42, Q43, Q44, Q45, Q46, Q47, Q48, Q49, Q50, Q51, Q52]), "radius" : 1 * mm, "tangentPropagation" : true, "allowEdgeOverflow" : false});
        }
        {
            var Q0;
            {var subQ0=sQuery(id+"F6.wireOp",EDGE,"E31");var subQ1=sQuery(id+"F6.wireOp",EDGE,"E13");var subQ2=makeQuery(id+"F6.imprint","INTERSECT",VERTEX,{"disambiguationData":[OD(0.0)],"derivedFrom":[subQ1,subQ0]});Q0=makeQuery(id+"F6.imprint","IMPRINT",FACE,{"disambiguationData":[TD([[makeQuery(id+"F6.imprint","IMPRINT",EDGE,{"disambiguationData":[TD([[subQ2,-1.0]])],"derivedFrom":subQ1}),-1.0]])]});}
            var Q1;
            {var subQ0=sQuery(id+"F6.wireOp",EDGE,"E31");var subQ1=sQuery(id+"F6.wireOp",EDGE,"E13");var subQ2=makeQuery(id+"F6.imprint","INTERSECT",VERTEX,{"disambiguationData":[OD(0.0)],"derivedFrom":[subQ1,subQ0]});Q1=makeQuery(id+"F6.imprint","IMPRINT",FACE,{"disambiguationData":[TD([[makeQuery(id+"F6.imprint","IMPRINT",EDGE,{"disambiguationData":[TD([[subQ2,-1.0]])],"derivedFrom":subQ1}),1.0]])]});}
            var Q2;
            {var subQ0=sQuery(id+"F6.wireOp",EDGE,"E32");var subQ1=sQuery(id+"F6.wireOp",EDGE,"E13");var subQ2=makeQuery(id+"F6.imprint","INTERSECT",VERTEX,{"disambiguationData":[OD(0.0)],"derivedFrom":[subQ1,subQ0]});Q2=makeQuery(id+"F6.imprint","IMPRINT",FACE,{"disambiguationData":[TD([[makeQuery(id+"F6.imprint","IMPRINT",EDGE,{"disambiguationData":[TD([[subQ2,-1.0]])],"derivedFrom":subQ1}),-1.0]])]});}
            var Q3;
            {var subQ0=sQuery(id+"F6.wireOp",EDGE,"E32");var subQ1=sQuery(id+"F6.wireOp",EDGE,"E13");var subQ2=makeQuery(id+"F6.imprint","INTERSECT",VERTEX,{"disambiguationData":[OD(0.0)],"derivedFrom":[subQ1,subQ0]});Q3=makeQuery(id+"F6.imprint","IMPRINT",FACE,{"disambiguationData":[TD([[makeQuery(id+"F6.imprint","IMPRINT",EDGE,{"disambiguationData":[TD([[subQ2,-1.0]])],"derivedFrom":subQ1}),1.0]])]});}
            var Q4;
            {var subQ0=sQuery(id+"F6.wireOp",EDGE,"E33");var subQ1=sQuery(id+"F6.wireOp",EDGE,"E13");var subQ2=makeQuery(id+"F6.imprint","INTERSECT",VERTEX,{"disambiguationData":[OD(0.0)],"derivedFrom":[subQ1,subQ0]});Q4=makeQuery(id+"F6.imprint","IMPRINT",FACE,{"disambiguationData":[TD([[makeQuery(id+"F6.imprint","IMPRINT",EDGE,{"disambiguationData":[TD([[subQ2,-1.0]])],"derivedFrom":subQ1}),1.0]])]});}
            var Q5;
            {var subQ0=sQuery(id+"F6.wireOp",EDGE,"E33");var subQ1=sQuery(id+"F6.wireOp",EDGE,"E13");var subQ2=makeQuery(id+"F6.imprint","INTERSECT",VERTEX,{"disambiguationData":[OD(0.0)],"derivedFrom":[subQ1,subQ0]});Q5=makeQuery(id+"F6.imprint","IMPRINT",FACE,{"disambiguationData":[TD([[makeQuery(id+"F6.imprint","IMPRINT",EDGE,{"disambiguationData":[TD([[subQ2,-1.0]])],"derivedFrom":subQ1}),-1.0]])]});}
            var Q6;
            {var subQ0=sQuery(id+"F6.wireOp",EDGE,"E34");var subQ1=sQuery(id+"F6.wireOp",EDGE,"E13");var subQ2=makeQuery(id+"F6.imprint","INTERSECT",VERTEX,{"disambiguationData":[OD(0.0)],"derivedFrom":[subQ1,subQ0]});Q6=makeQuery(id+"F6.imprint","IMPRINT",FACE,{"disambiguationData":[TD([[makeQuery(id+"F6.imprint","IMPRINT",EDGE,{"disambiguationData":[TD([[subQ2,-1.0]])],"derivedFrom":subQ1}),1.0]])]});}
            var Q7;
            {var subQ0=sQuery(id+"F6.wireOp",EDGE,"E34");var subQ1=sQuery(id+"F6.wireOp",EDGE,"E13");var subQ2=makeQuery(id+"F6.imprint","INTERSECT",VERTEX,{"disambiguationData":[OD(0.0)],"derivedFrom":[subQ1,subQ0]});Q7=makeQuery(id+"F6.imprint","IMPRINT",FACE,{"disambiguationData":[TD([[makeQuery(id+"F6.imprint","IMPRINT",EDGE,{"disambiguationData":[TD([[subQ2,-1.0]])],"derivedFrom":subQ1}),-1.0]])]});}
            var Q8;
            {var subQ1=sQuery(id+"F6.wireOp",EDGE,"E36.bottom");Q8=makeQuery(id+"F6.imprint","IMPRINT",FACE,{"disambiguationData":[TD([[makeQuery(id+"F6.imprint","IMPRINT",EDGE,{"derivedFrom":subQ1}),-1.0]])]});}
            var Q9;
            {var subQ0=sQuery(id+"F6.wireOp",EDGE,"E36.top");var subQ1=sQuery(id+"F6.wireOp",EDGE,"E13");var subQ2=makeQuery(id+"F6.imprint","INTERSECT",VERTEX,{"derivedFrom":[subQ1,subQ0]});Q9=makeQuery(id+"F6.imprint","IMPRINT",FACE,{"disambiguationData":[TD([[makeQuery(id+"F6.imprint","IMPRINT",EDGE,{"disambiguationData":[TD([[subQ2,-1.0]])],"derivedFrom":subQ1}),1.0]])]});}
            var Q10;
            {var subQ0=sQuery(id+"F6.wireOp",EDGE,"E35");var subQ1=sQuery(id+"F6.wireOp",EDGE,"E13");var subQ2=makeQuery(id+"F6.imprint","INTERSECT",VERTEX,{"disambiguationData":[OD(0.0)],"derivedFrom":[subQ1,subQ0]});Q10=makeQuery(id+"F6.imprint","IMPRINT",FACE,{"disambiguationData":[TD([[makeQuery(id+"F6.imprint","IMPRINT",EDGE,{"disambiguationData":[TD([[subQ2,-1.0]])],"derivedFrom":subQ1}),-1.0]])]});}
            var Q11;
            {var subQ0=sQuery(id+"F6.wireOp",EDGE,"E35");var subQ1=sQuery(id+"F6.wireOp",EDGE,"E13");var subQ2=makeQuery(id+"F6.imprint","INTERSECT",VERTEX,{"disambiguationData":[OD(0.0)],"derivedFrom":[subQ1,subQ0]});Q11=makeQuery(id+"F6.imprint","IMPRINT",FACE,{"disambiguationData":[TD([[makeQuery(id+"F6.imprint","IMPRINT",EDGE,{"disambiguationData":[TD([[subQ2,-1.0]])],"derivedFrom":subQ1}),1.0]])]});}
            extrude(context, id + "F9", {"entities" : qUnion([Q0, Q1, Q2, Q3, Q4, Q5, Q6, Q7, Q8, Q9, Q10, Q11]), "operationType" : NewBodyOperationType.ADD, "depth" : 11 * mm, "offsetDistance" : 25 * mm, "hasDraft" : true, "draftAngle" : .9 * degree, "draftPullDirection" : true});
        }
        {
            var Q0;
            Q0=makeQuery(id+"F9.opExtrude","CAP_EDGE",EDGE,{"disambiguationData":[OSD([sQuery(id+"F6.wireOp",EDGE,"E35")])],"isStart":false});
            var Q1;
            Q1=makeQuery(id+"F9.opExtrude","CAP_FACE",FACE,{"disambiguationData":[OSD([sQuery(id+"F6.wireOp",EDGE,"E31")])],"isStart":false});
            var Q2;
            Q2=makeQuery(id+"F9.opExtrude","CAP_FACE",FACE,{"disambiguationData":[OSD([sQuery(id+"F6.wireOp",EDGE,"E32")])],"isStart":false});
            var Q3;
            Q3=makeQuery(id+"F9.opExtrude","CAP_FACE",FACE,{"disambiguationData":[OSD([sQuery(id+"F6.wireOp",EDGE,"E33")])],"isStart":false});
            var Q4;
            Q4=makeQuery(id+"F9.opExtrude","CAP_FACE",FACE,{"disambiguationData":[OSD([sQuery(id+"F6.wireOp",EDGE,"E34")])],"isStart":false});
            var Q5;
            Q5=makeQuery(id+"F9.opExtrude","CAP_EDGE",EDGE,{"disambiguationData":[OSD([sQuery(id+"F6.wireOp",EDGE,"E36.left")])],"isStart":false});
            var Q6;
            Q6=makeQuery(id+"F9.opExtrude","CAP_EDGE",EDGE,{"disambiguationData":[OSD([sQuery(id+"F6.wireOp",EDGE,"E36.right")])],"isStart":false});
            var Q7;
            Q7=makeQuery(id+"F9.opExtrude","CAP_EDGE",EDGE,{"disambiguationData":[OSD([sQuery(id+"F6.wireOp",EDGE,"E36.bottom")])],"isStart":false});
            var Q8;
            Q8=makeQuery(id+"F9.opExtrude","CAP_EDGE",EDGE,{"disambiguationData":[OSD([sQuery(id+"F6.wireOp",EDGE,"E36.top")])],"isStart":false});
            fillet(context, id + "F10", {"entities" : qUnion([Q0, Q1, Q2, Q3, Q4, Q5, Q6, Q7, Q8]), "radius" : .45 * mm, "tangentPropagation" : true, "allowEdgeOverflow" : false});
        }
        {
            var Q0;
            {var subQ0=sQuery(id+"F6.wireOp",EDGE,"E35");var subQ1=sQuery(id+"F6.wireOp",EDGE,"E13");var subQ2=makeQuery(id+"F6.imprint","INTERSECT",VERTEX,{"disambiguationData":[OD(0.0)],"derivedFrom":[subQ1,subQ0]});Q0=makeQuery(id+"F6.imprint","IMPRINT",FACE,{"disambiguationData":[TD([[makeQuery(id+"F6.imprint","IMPRINT",EDGE,{"disambiguationData":[TD([[subQ2,-1.0]])],"derivedFrom":subQ1}),-1.0]])]});}
            var Q1;
            {var subQ0=sQuery(id+"F6.wireOp",EDGE,"E35");var subQ1=sQuery(id+"F6.wireOp",EDGE,"E13");var subQ2=makeQuery(id+"F6.imprint","INTERSECT",VERTEX,{"disambiguationData":[OD(0.0)],"derivedFrom":[subQ1,subQ0]});Q1=makeQuery(id+"F6.imprint","IMPRINT",FACE,{"disambiguationData":[TD([[makeQuery(id+"F6.imprint","IMPRINT",EDGE,{"disambiguationData":[TD([[subQ2,-1.0]])],"derivedFrom":subQ1}),1.0]])]});}
            var Q2;
            {var subQ1=sQuery(id+"F6.wireOp",EDGE,"E36.bottom");Q2=makeQuery(id+"F6.imprint","IMPRINT",FACE,{"disambiguationData":[TD([[makeQuery(id+"F6.imprint","IMPRINT",EDGE,{"derivedFrom":subQ1}),-1.0]])]});}
            var Q3;
            {var subQ0=sQuery(id+"F6.wireOp",EDGE,"E36.top");var subQ1=sQuery(id+"F6.wireOp",EDGE,"E13");var subQ2=makeQuery(id+"F6.imprint","INTERSECT",VERTEX,{"derivedFrom":[subQ1,subQ0]});Q3=makeQuery(id+"F6.imprint","IMPRINT",FACE,{"disambiguationData":[TD([[makeQuery(id+"F6.imprint","IMPRINT",EDGE,{"disambiguationData":[TD([[subQ2,-1.0]])],"derivedFrom":subQ1}),1.0]])]});}
            var Q4;
            {var subQ0=sQuery(id+"F6.wireOp",EDGE,"E34");var subQ1=sQuery(id+"F6.wireOp",EDGE,"E13");var subQ2=makeQuery(id+"F6.imprint","INTERSECT",VERTEX,{"disambiguationData":[OD(0.0)],"derivedFrom":[subQ1,subQ0]});Q4=makeQuery(id+"F6.imprint","IMPRINT",FACE,{"disambiguationData":[TD([[makeQuery(id+"F6.imprint","IMPRINT",EDGE,{"disambiguationData":[TD([[subQ2,-1.0]])],"derivedFrom":subQ1}),1.0]])]});}
            var Q5;
            {var subQ0=sQuery(id+"F6.wireOp",EDGE,"E34");var subQ1=sQuery(id+"F6.wireOp",EDGE,"E13");var subQ2=makeQuery(id+"F6.imprint","INTERSECT",VERTEX,{"disambiguationData":[OD(0.0)],"derivedFrom":[subQ1,subQ0]});Q5=makeQuery(id+"F6.imprint","IMPRINT",FACE,{"disambiguationData":[TD([[makeQuery(id+"F6.imprint","IMPRINT",EDGE,{"disambiguationData":[TD([[subQ2,-1.0]])],"derivedFrom":subQ1}),-1.0]])]});}
            var Q6;
            {var subQ0=sQuery(id+"F6.wireOp",EDGE,"E33");var subQ1=sQuery(id+"F6.wireOp",EDGE,"E13");var subQ2=makeQuery(id+"F6.imprint","INTERSECT",VERTEX,{"disambiguationData":[OD(0.0)],"derivedFrom":[subQ1,subQ0]});Q6=makeQuery(id+"F6.imprint","IMPRINT",FACE,{"disambiguationData":[TD([[makeQuery(id+"F6.imprint","IMPRINT",EDGE,{"disambiguationData":[TD([[subQ2,-1.0]])],"derivedFrom":subQ1}),1.0]])]});}
            var Q7;
            {var subQ0=sQuery(id+"F6.wireOp",EDGE,"E33");var subQ1=sQuery(id+"F6.wireOp",EDGE,"E13");var subQ2=makeQuery(id+"F6.imprint","INTERSECT",VERTEX,{"disambiguationData":[OD(0.0)],"derivedFrom":[subQ1,subQ0]});Q7=makeQuery(id+"F6.imprint","IMPRINT",FACE,{"disambiguationData":[TD([[makeQuery(id+"F6.imprint","IMPRINT",EDGE,{"disambiguationData":[TD([[subQ2,-1.0]])],"derivedFrom":subQ1}),-1.0]])]});}
            var Q8;
            {var subQ0=sQuery(id+"F6.wireOp",EDGE,"E32");var subQ1=sQuery(id+"F6.wireOp",EDGE,"E13");var subQ2=makeQuery(id+"F6.imprint","INTERSECT",VERTEX,{"disambiguationData":[OD(0.0)],"derivedFrom":[subQ1,subQ0]});Q8=makeQuery(id+"F6.imprint","IMPRINT",FACE,{"disambiguationData":[TD([[makeQuery(id+"F6.imprint","IMPRINT",EDGE,{"disambiguationData":[TD([[subQ2,-1.0]])],"derivedFrom":subQ1}),1.0]])]});}
            var Q9;
            {var subQ0=sQuery(id+"F6.wireOp",EDGE,"E32");var subQ1=sQuery(id+"F6.wireOp",EDGE,"E13");var subQ2=makeQuery(id+"F6.imprint","INTERSECT",VERTEX,{"disambiguationData":[OD(0.0)],"derivedFrom":[subQ1,subQ0]});Q9=makeQuery(id+"F6.imprint","IMPRINT",FACE,{"disambiguationData":[TD([[makeQuery(id+"F6.imprint","IMPRINT",EDGE,{"disambiguationData":[TD([[subQ2,-1.0]])],"derivedFrom":subQ1}),-1.0]])]});}
            var Q10;
            {var subQ0=sQuery(id+"F6.wireOp",EDGE,"E31");var subQ1=sQuery(id+"F6.wireOp",EDGE,"E13");var subQ2=makeQuery(id+"F6.imprint","INTERSECT",VERTEX,{"disambiguationData":[OD(0.0)],"derivedFrom":[subQ1,subQ0]});Q10=makeQuery(id+"F6.imprint","IMPRINT",FACE,{"disambiguationData":[TD([[makeQuery(id+"F6.imprint","IMPRINT",EDGE,{"disambiguationData":[TD([[subQ2,-1.0]])],"derivedFrom":subQ1}),-1.0]])]});}
            var Q11;
            {var subQ0=sQuery(id+"F6.wireOp",EDGE,"E31");var subQ1=sQuery(id+"F6.wireOp",EDGE,"E13");var subQ2=makeQuery(id+"F6.imprint","INTERSECT",VERTEX,{"disambiguationData":[OD(0.0)],"derivedFrom":[subQ1,subQ0]});Q11=makeQuery(id+"F6.imprint","IMPRINT",FACE,{"disambiguationData":[TD([[makeQuery(id+"F6.imprint","IMPRINT",EDGE,{"disambiguationData":[TD([[subQ2,-1.0]])],"derivedFrom":subQ1}),1.0]])]});}
            extrude(context, id + "F11", {"entities" : qUnion([Q0, Q1, Q2, Q3, Q4, Q5, Q6, Q7, Q8, Q9, Q10, Q11]), "operationType" : NewBodyOperationType.REMOVE, "depth" : 3 * mm, "offsetDistance" : 25 * mm});
        }
        {
            var Q0;
            Q0=qCreatedBy(makeId("Top.planeOp"),FACE);
            var sketch = newSketch(context, id + "F12", { "sketchPlane" : qUnion([Q0])});
            skCircle(sketch, "E37", {"center": v(0, 0) * mm, "radius": 17.33 * mm});
            skSolve(sketch);
        }
        {
            var Q0;
            Q0=makeQuery(id+"F12.imprint","IMPRINT",FACE,{"disambiguationData":[TD([[makeQuery(id+"F12.imprint","IMPRINT",EDGE,{"derivedFrom":sQuery(id+"F12.wireOp",EDGE,"E37")}),1.0]])]});
            extrude(context, id + "F13", {"entities" : qUnion([Q0]), "operationType" : NewBodyOperationType.REMOVE, "depth" : 1 * mm, "offsetDistance" : 25 * mm});
        }
    });
